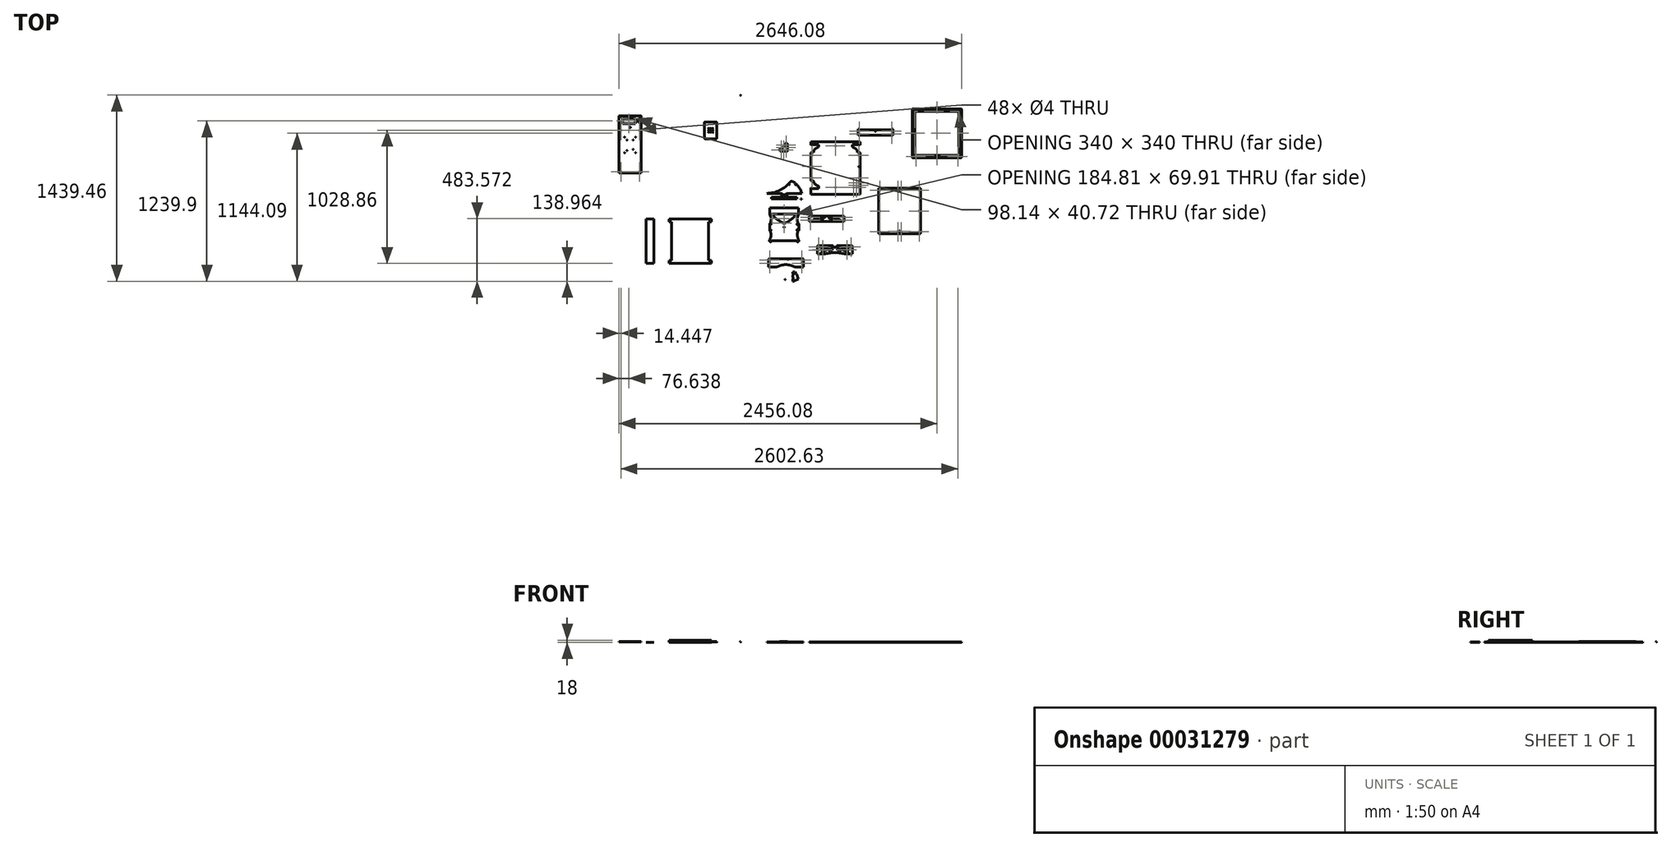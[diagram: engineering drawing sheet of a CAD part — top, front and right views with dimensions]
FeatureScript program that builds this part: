
annotation { "Feature Type Name" : "Feature", "Feature Type Description" : "" }
export const myFeature = defineFeature(function(context is Context, id is Id, definition is map)
    precondition{}
    {
        {
            var Q0;
            Q0=qCreatedBy(makeId("Top.planeOp"),FACE);
            var sketch = newSketch(context, id + "F0", { "sketchPlane" : qUnion([Q0])});
            skLineSegment(sketch, "E0", {"start": v(-196.4, -19.93) * mm, "end": v(-196.4, 30.07) * mm});
            skCircle(sketch, "E1", {"center": v(-187.75, 27.57) * mm, "radius": 2.75 * mm});
            skCircle(sketch, "E2", {"center": v(-187.75, -17.43) * mm, "radius": 2.75 * mm});
            skArc(sketch, "E3", {"start": v(-196.4, -19.93) * mm, "mid": v(-194.93, -23.47) * mm, "end": v(-191.4, -24.93) * mm});
            skArc(sketch, "E4", {"start": v(-191.4, 35.07) * mm, "mid": v(-194.93, 33.6) * mm, "end": v(-196.4, 30.07) * mm});
            skLineSegment(sketch, "E5", {"start": v(28.6, 30.07) * mm, "end": v(28.6, -19.93) * mm});
            skCircle(sketch, "E6", {"center": v(19.95, 27.57) * mm, "radius": 5.08 * mm});
            skCircle(sketch, "E7", {"center": v(19.95, -17.43) * mm, "radius": 5.08 * mm});
            skLineSegment(sketch, "E8.trimOffspring", {"start": v(14.88, 27.57) * mm, "end": v(19.95, 27.57) * mm});
            skPoint(sketch, "E9.visualSharp", {"position": v(28.6, 35.07) * mm});
            skArc(sketch, "E9.filletArc", {"start": v(28.6, 30.07) * mm, "mid": v(27.14, 33.6) * mm, "end": v(23.6, 35.07) * mm});
            skPoint(sketch, "E10.visualSharp", {"position": v(28.6, -24.93) * mm});
            skArc(sketch, "E10.filletArc", {"start": v(23.6, -24.93) * mm, "mid": v(27.14, -23.47) * mm, "end": v(28.6, -19.93) * mm});
            skCircle(sketch, "E11", {"center": v(-83.9, 5.07) * mm, "radius": 3.2 * mm});
            skLineSegment(sketch, "E12", {"start": v(-87.4, 19.55) * mm, "end": v(-80.33, 19.55) * mm});
            skLineSegment(sketch, "E13", {"start": v(-87.4, 21.55) * mm, "end": v(-80.33, 21.55) * mm});
            skLineSegment(sketch, "E14", {"start": v(-87.4, 23.86) * mm, "end": v(-80.32, 23.86) * mm});
            skLineSegment(sketch, "E15", {"start": v(-87.4, 25.86) * mm, "end": v(-80.32, 25.86) * mm});
            skLineSegment(sketch, "E16", {"start": v(-87.4, 27.93) * mm, "end": v(-80.32, 27.92) * mm});
            skLineSegment(sketch, "E17", {"start": v(-87.4, 31.34) * mm, "end": v(-80.31, 31.33) * mm});
            skLineSegment(sketch, "E18", {"start": v(-87.4, -9.95) * mm, "end": v(-80.38, -9.95) * mm});
            skLineSegment(sketch, "E19", {"start": v(-87.4, -11.95) * mm, "end": v(-80.38, -11.95) * mm});
            skLineSegment(sketch, "E20", {"start": v(-87.4, -16.14) * mm, "end": v(-80.39, -16.14) * mm});
            skLineSegment(sketch, "E21", {"start": v(-87.4, -14.14) * mm, "end": v(-80.39, -14.14) * mm});
            skLineSegment(sketch, "E22", {"start": v(-87.4, -21.89) * mm, "end": v(-80.4, -21.89) * mm});
            skLineSegment(sketch, "E23", {"start": v(-87.4, -18.45) * mm, "end": v(-80.4, -18.45) * mm});
            skLineSegment(sketch, "E24", {"start": v(-83.9, -21.89) * mm, "end": v(-80.4, -21.89) * mm});
            skLineSegment(sketch, "E25", {"start": v(-83.9, -21.89) * mm, "end": v(-87.4, -21.89) * mm});
            skLineSegment(sketch, "E26", {"start": v(-87.4, -21.89) * mm, "end": v(-87.4, -18.45) * mm});
            skLineSegment(sketch, "E27", {"start": v(-80.4, -21.89) * mm, "end": v(-80.4, -18.45) * mm});
            skLineSegment(sketch, "E28.trimOffspring", {"start": v(-87.4, 19.55) * mm, "end": v(-87.4, 21.55) * mm});
            skLineSegment(sketch, "E29.trimOffspring", {"start": v(-80.33, 19.55) * mm, "end": v(-80.33, 21.55) * mm});
            skLineSegment(sketch, "E30.trimOffspring", {"start": v(-80.32, 27.92) * mm, "end": v(-80.31, 31.34) * mm});
            skLineSegment(sketch, "E31.trimOffspring", {"start": v(-87.4, 27.93) * mm, "end": v(-87.4, 31.34) * mm});
            skLineSegment(sketch, "E32.trimOffspring", {"start": v(-87.4, 23.86) * mm, "end": v(-87.4, 25.86) * mm});
            skLineSegment(sketch, "E33.trimOffspring", {"start": v(-80.32, 23.86) * mm, "end": v(-80.32, 25.86) * mm});
            skLineSegment(sketch, "E34.trimOffspring", {"start": v(-87.4, -16.14) * mm, "end": v(-87.4, -14.14) * mm});
            skPoint(sketch, "E35.trimOffspring.end.orphan", {"position": v(-83.9, -24.93) * mm});
            skLineSegment(sketch, "E36.trimOffspring", {"start": v(-80.39, -16.14) * mm, "end": v(-80.39, -14.14) * mm});
            skLineSegment(sketch, "E37.trimOffspring", {"start": v(-87.4, -11.95) * mm, "end": v(-87.4, -9.95) * mm});
            skLineSegment(sketch, "E38.trimOffspring", {"start": v(-80.38, -11.95) * mm, "end": v(-80.38, -9.95) * mm});
            skCircle(sketch, "E39", {"center": v(-188.4, 109.57) * mm, "radius": 1.5 * mm});
            skCircle(sketch, "E40", {"center": v(20.6, 109.57) * mm, "radius": 1.5 * mm});
            skCircle(sketch, "E41", {"center": v(-188.4, -99.43) * mm, "radius": 1.5 * mm});
            skCircle(sketch, "E42", {"center": v(20.6, -99.43) * mm, "radius": 1.5 * mm});
            skLineSegment(sketch, "E43.MirrorCS", {"start": v(28.6, -19.93) * mm, "end": v(28.6, 30.07) * mm});
            skArc(sketch, "E44", {"start": v(-196.14, -94.85) * mm, "mid": v(-190.78, -108.11) * mm, "end": v(-179.4, -99.43) * mm});
            skArc(sketch, "E45", {"start": v(11.6, -99.43) * mm, "mid": v(22.98, -108.11) * mm, "end": v(28.34, -94.85) * mm});
            skArc(sketch, "E46", {"start": v(28.34, 104.98) * mm, "mid": v(22.98, 118.25) * mm, "end": v(11.6, 109.57) * mm});
            skArc(sketch, "E47", {"start": v(-179.4, 109.57) * mm, "mid": v(-190.78, 118.25) * mm, "end": v(-196.14, 104.98) * mm});
            skArc(sketch, "E48", {"start": v(-196.14, -94.85) * mm, "mid": v(-185.98, -60.42) * mm, "end": v(-191.4, -24.93) * mm});
            skArc(sketch, "E49", {"start": v(-83.9, -24.93) * mm, "mid": v(-137.85, -54.24) * mm, "end": v(-179.4, -99.43) * mm});
            skArc(sketch, "E50.MirrorCS", {"start": v(-83.9, -24.93) * mm, "mid": v(-29.95, -54.24) * mm, "end": v(11.6, -99.43) * mm});
            skArc(sketch, "E51.MirrorCS", {"start": v(28.34, -94.85) * mm, "mid": v(18.18, -60.42) * mm, "end": v(23.6, -24.93) * mm});
            skArc(sketch, "E52.MirrorCS", {"start": v(-83.9, 35.07) * mm, "mid": v(-137.85, 64.37) * mm, "end": v(-179.4, 109.57) * mm});
            skArc(sketch, "E53.MirrorCS", {"start": v(-196.14, 104.98) * mm, "mid": v(-185.98, 70.55) * mm, "end": v(-191.4, 35.07) * mm});
            skArc(sketch, "E54.MirrorCS", {"start": v(-83.9, 35.07) * mm, "mid": v(-29.95, 64.37) * mm, "end": v(11.6, 109.57) * mm});
            skArc(sketch, "E55.MirrorCS", {"start": v(28.34, 104.98) * mm, "mid": v(18.18, 70.55) * mm, "end": v(23.6, 35.07) * mm});
            skLineSegment(sketch, "E56.trimOffspring", {"start": v(-196.4, 5.07) * mm, "end": v(-227.61, 5.07) * mm});
            skLineSegment(sketch, "E57", {"start": v(-179.4, -99.43) * mm, "end": v(11.6, -99.43) * mm});
            skLineSegment(sketch, "E58", {"start": v(-179.4, 109.57) * mm, "end": v(11.6, 109.57) * mm});
            skLineSegment(sketch, "E59.bottom", {"start": v(-196.14, 104.98) * mm, "end": v(28.34, 104.98) * mm});
            skLineSegment(sketch, "E59.top", {"start": v(-196.14, 155.03) * mm, "end": v(28.34, 155.03) * mm});
            skLineSegment(sketch, "E59.left", {"start": v(-196.14, 104.98) * mm, "end": v(-196.14, 155.03) * mm});
            skLineSegment(sketch, "E59.right", {"start": v(28.34, 104.98) * mm, "end": v(28.34, 155.03) * mm});
            skSolve(sketch);
        }
        {
            var Q0;
            Q0=makeQuery(id+"F0.imprint","IMPRINT",FACE,{"disambiguationData":[TD([[makeQuery(id+"F0.imprint","IMPRINT",EDGE,{"derivedFrom":sQuery(id+"F0.wireOp",EDGE,"E0")}),-1.0]])]});
            var Q1;
            Q1=makeQuery(id+"F0.imprint","IMPRINT",FACE,{"disambiguationData":[TD([[makeQuery(id+"F0.imprint","IMPRINT",EDGE,{"derivedFrom":sQuery(id+"F0.wireOp",EDGE,"E23")}),-1.0]])]});
            var Q2;
            Q2=makeQuery(id+"F0.imprint","IMPRINT",FACE,{"disambiguationData":[TD([[makeQuery(id+"F0.imprint","IMPRINT",EDGE,{"derivedFrom":sQuery(id+"F0.wireOp",EDGE,"E49")}),1.0]])]});
            var Q3;
            Q3=makeQuery(id+"F0.imprint","IMPRINT",FACE,{"disambiguationData":[TD([[makeQuery(id+"F0.imprint","IMPRINT",EDGE,{"derivedFrom":sQuery(id+"F0.wireOp",EDGE,"E18")}),-1.0]])]});
            var Q4;
            Q4=makeQuery(id+"F0.imprint","IMPRINT",FACE,{"disambiguationData":[TD([[makeQuery(id+"F0.imprint","IMPRINT",EDGE,{"derivedFrom":sQuery(id+"F0.wireOp",EDGE,"E20")}),1.0]])]});
            var Q5;
            Q5=makeQuery(id+"F0.imprint","IMPRINT",FACE,{"disambiguationData":[TD([[makeQuery(id+"F0.imprint","IMPRINT",EDGE,{"derivedFrom":sQuery(id+"F0.wireOp",EDGE,"E52.MirrorCS")}),-1.0]])]});
            var Q6;
            Q6=makeQuery(id+"F0.imprint","IMPRINT",FACE,{"disambiguationData":[TD([[makeQuery(id+"F0.imprint","IMPRINT",EDGE,{"derivedFrom":sQuery(id+"F0.wireOp",EDGE,"E12")}),1.0]])]});
            var Q7;
            Q7=makeQuery(id+"F0.imprint","IMPRINT",FACE,{"disambiguationData":[TD([[makeQuery(id+"F0.imprint","IMPRINT",EDGE,{"derivedFrom":sQuery(id+"F0.wireOp",EDGE,"E14")}),1.0]])]});
            var Q8;
            {var subQ2=sQuery(id+"F0.wireOp",EDGE,"E16");Q8=makeQuery(id+"F0.imprint","IMPRINT",FACE,{"disambiguationData":[TD([[makeQuery(id+"F0.imprint","IMPRINT",EDGE,{"derivedFrom":subQ2}),1.0]])]});}
            var Q9;
            {var subQ7=sQuery(id+"F0.wireOp",EDGE,"E58");Q9=makeQuery(id+"F0.imprint","IMPRINT",FACE,{"disambiguationData":[TD([[makeQuery(id+"F0.imprint","IMPRINT",EDGE,{"derivedFrom":subQ7}),1.0]])]});}
            var Q10;
            Q10=makeQuery(id+"F0.imprint","IMPRINT",FACE,{"disambiguationData":[TD([[makeQuery(id+"F0.imprint","IMPRINT",EDGE,{"derivedFrom":sQuery(id+"F0.wireOp",EDGE,"E40")}),-1.0]])]});
            var Q11;
            Q11=makeQuery(id+"F0.imprint","IMPRINT",FACE,{"disambiguationData":[TD([[makeQuery(id+"F0.imprint","IMPRINT",EDGE,{"derivedFrom":sQuery(id+"F0.wireOp",EDGE,"E39")}),-1.0]])]});
            var Q12;
            {var subQ5=sQuery(id+"F0.wireOp",EDGE,"E58");Q12=makeQuery(id+"F0.imprint","IMPRINT",FACE,{"disambiguationData":[TD([[makeQuery(id+"F0.imprint","IMPRINT",EDGE,{"derivedFrom":subQ5}),-1.0]])]});}
            extrude(context, id + "F1", {"entities" : qUnion([Q0, Q1, Q2, Q3, Q4, Q5, Q6, Q7, Q8, Q9, Q10, Q11, Q12]), "depth" : 4 * mm});
        }
        {
            var Q0;
            Q0=qCreatedBy(makeId("Top.planeOp"),FACE);
            var sketch = newSketch(context, id + "F2", { "sketchPlane" : qUnion([Q0])});
            skLineSegment(sketch, "E60", {"start": v(-104.69, 266.67) * mm, "end": v(-62.63, 266.67) * mm});
            skLineSegment(sketch, "E61", {"start": v(-62.63, 266.67) * mm, "end": v(-62.63, 266.67) * mm});
            skLineSegment(sketch, "E62", {"start": v(-62.63, 266.67) * mm, "end": v(51.38, 266.67) * mm});
            skLineSegment(sketch, "E63", {"start": v(51.38, 266.67) * mm, "end": v(51.38, 224.88) * mm});
            skLineSegment(sketch, "E64", {"start": v(51.38, 224.88) * mm, "end": v(41.38, 224.88) * mm});
            skLineSegment(sketch, "E65", {"start": v(41.38, 224.88) * mm, "end": v(51.38, 224.88) * mm});
            skLineSegment(sketch, "E66.bottom", {"start": v(-104.69, 266.67) * mm, "end": v(-62.62, 266.67) * mm});
            skLineSegment(sketch, "E66.right", {"start": v(-62.62, 266.67) * mm, "end": v(-62.62, 224.88) * mm});
            skLineSegment(sketch, "E67", {"start": v(-104.69, 224.88) * mm, "end": v(-62.62, 224.88) * mm});
            skLineSegment(sketch, "E68", {"start": v(-62.62, 224.88) * mm, "end": v(41.38, 224.88) * mm});
            skLineSegment(sketch, "E69", {"start": v(-104.69, 224.88) * mm, "end": v(-104.69, 266.67) * mm});
            skCircle(sketch, "E70", {"center": v(41.38, 258.88) * mm, "radius": 2 * mm});
            skCircle(sketch, "E71", {"center": v(41.38, 234.88) * mm, "radius": 2 * mm});
            skCircle(sketch, "E72", {"center": v(-83.65, 245.28) * mm, "radius": 11.05 * mm});
            skCircle(sketch, "E73", {"center": v(-99.2, 229.73) * mm, "radius": 1.65 * mm});
            skCircle(sketch, "E74", {"center": v(-68.1, 229.79) * mm, "radius": 1.65 * mm});
            skCircle(sketch, "E75", {"center": v(-99.2, 260.83) * mm, "radius": 1.65 * mm});
            skCircle(sketch, "E76", {"center": v(-68.1, 261) * mm, "radius": 1.65 * mm});
            skLineSegment(sketch, "E77", {"start": v(-83.66, 224.88) * mm, "end": v(-83.66, 266.67) * mm});
            skLineSegment(sketch, "E78.MirrorCS", {"start": v(-104.69, 224.88) * mm, "end": v(-208.69, 224.88) * mm});
            skLineSegment(sketch, "E79.MirrorCS", {"start": v(-104.69, 266.67) * mm, "end": v(-218.69, 266.67) * mm});
            skLineSegment(sketch, "E80.MirrorCS", {"start": v(-218.69, 266.67) * mm, "end": v(-218.69, 224.88) * mm});
            skLineSegment(sketch, "E81.MirrorCS", {"start": v(-208.69, 224.88) * mm, "end": v(-210.69, 224.88) * mm});
            skCircle(sketch, "E82.MirrorC", {"center": v(-208.69, 234.88) * mm, "radius": 2 * mm});
            skCircle(sketch, "E83.MirrorC", {"center": v(-208.69, 258.88) * mm, "radius": 2 * mm});
            skLineSegment(sketch, "E84.bottom", {"start": v(-83.66, 224.88) * mm, "end": v(-181, 224.88) * mm});
            skLineSegment(sketch, "E84.top", {"start": v(-83.66, 237.25) * mm, "end": v(-181, 237.25) * mm});
            skLineSegment(sketch, "E84.left", {"start": v(-83.66, 224.88) * mm, "end": v(-83.66, 237.25) * mm});
            skLineSegment(sketch, "E84.right", {"start": v(-181, 224.88) * mm, "end": v(-181, 237.25) * mm});
            skLineSegment(sketch, "E85.MirrorCS", {"start": v(-83.66, 237.25) * mm, "end": v(13.7, 237.25) * mm});
            skLineSegment(sketch, "E86.MirrorCS", {"start": v(13.7, 224.88) * mm, "end": v(13.7, 237.25) * mm});
            skCircle(sketch, "E87", {"center": v(3.35, 260.88) * mm, "radius": 1.5 * mm});
            skCircle(sketch, "E88", {"center": v(-44.47, 253.5) * mm, "radius": 1.5 * mm});
            skCircle(sketch, "E89", {"center": v(-44.78, 334.21) * mm, "radius": 1.5 * mm});
            skCircle(sketch, "E90", {"center": v(3.26, 334.22) * mm, "radius": 1.5 * mm});
            skArc(sketch, "E91", {"start": v(51.38, 266.67) * mm, "mid": v(26.53, 319.96) * mm, "end": v(-18.2, 358.13) * mm});
            skArc(sketch, "E92", {"start": v(-218.69, 266.67) * mm, "mid": v(-117.85, 289.71) * mm, "end": v(-37.02, 354.25) * mm});
            skArc(sketch, "E93.filletArc", {"start": v(-18.2, 358.13) * mm, "mid": v(-28.3, 359.6) * mm, "end": v(-37.02, 354.25) * mm});
            skLineSegment(sketch, "E94", {"start": v(-218.69, 224.88) * mm, "end": v(-218.69, 220.88) * mm});
            skLineSegment(sketch, "E95", {"start": v(-218.69, 220.88) * mm, "end": v(-210.69, 220.88) * mm});
            skLineSegment(sketch, "E96", {"start": v(-210.69, 220.88) * mm, "end": v(-210.69, 224.88) * mm});
            skLineSegment(sketch, "E97.MirrorCS", {"start": v(51.38, 224.88) * mm, "end": v(51.38, 220.88) * mm});
            skLineSegment(sketch, "E98.MirrorCS", {"start": v(43.38, 220.88) * mm, "end": v(43.38, 224.88) * mm});
            skLineSegment(sketch, "E99.MirrorCS", {"start": v(51.38, 220.88) * mm, "end": v(43.38, 220.88) * mm});
            skPoint(sketch, "E100.orphan", {"position": v(-218.69, 224.88) * mm});
            skSolve(sketch);
        }
        {
            var Q0;
            {var subQ8=sQuery(id+"F2.wireOp",EDGE,"E62");Q0=makeQuery(id+"F2.imprint","IMPRINT",FACE,{"disambiguationData":[TD([[makeQuery(id+"F2.imprint","IMPRINT",EDGE,{"derivedFrom":subQ8}),1.0]])]});}
            var Q1;
            Q1=makeQuery(id+"F2.imprint","IMPRINT",FACE,{"disambiguationData":[TD([[makeQuery(id+"F2.imprint","IMPRINT",EDGE,{"derivedFrom":sQuery(id+"F2.wireOp",EDGE,"E78.MirrorCS")}),-1.0]])]});
            var Q2;
            Q2=makeQuery(id+"F2.imprint","IMPRINT",FACE,{"disambiguationData":[TD([[makeQuery(id+"F2.imprint","IMPRINT",EDGE,{"derivedFrom":sQuery(id+"F2.wireOp",EDGE,"E73")}),-1.0]])]});
            var Q3;
            Q3=makeQuery(id+"F2.imprint","IMPRINT",FACE,{"disambiguationData":[TD([[makeQuery(id+"F2.imprint","IMPRINT",EDGE,{"derivedFrom":sQuery(id+"F2.wireOp",EDGE,"E74")}),-1.0]])]});
            var Q4;
            {var subQ1=sQuery(id+"F2.wireOp",EDGE,"E97.MirrorCS");Q4=makeQuery(id+"F2.imprint","IMPRINT",FACE,{"disambiguationData":[TD([[makeQuery(id+"F2.imprint","IMPRINT",EDGE,{"derivedFrom":subQ1}),-1.0]])]});}
            var Q5;
            Q5=makeQuery(id+"F2.imprint","IMPRINT",FACE,{"disambiguationData":[TD([[makeQuery(id+"F2.imprint","IMPRINT",EDGE,{"derivedFrom":sQuery(id+"F2.wireOp",EDGE,"E75")}),-1.0]])]});
            var Q6;
            Q6=makeQuery(id+"F2.imprint","IMPRINT",FACE,{"disambiguationData":[TD([[makeQuery(id+"F2.imprint","IMPRINT",EDGE,{"derivedFrom":sQuery(id+"F2.wireOp",EDGE,"E76")}),-1.0]])]});
            var Q7;
            {var subQ5=sQuery(id+"F2.wireOp",EDGE,"E86.MirrorCS");Q7=makeQuery(id+"F2.imprint","IMPRINT",FACE,{"disambiguationData":[TD([[makeQuery(id+"F2.imprint","IMPRINT",EDGE,{"derivedFrom":subQ5}),1.0]])]});}
            var Q8;
            {var subQ5=sQuery(id+"F2.wireOp",EDGE,"E84.right");Q8=makeQuery(id+"F2.imprint","IMPRINT",FACE,{"disambiguationData":[TD([[makeQuery(id+"F2.imprint","IMPRINT",EDGE,{"derivedFrom":subQ5}),-1.0]])]});}
            var Q9;
            {var subQ7=sQuery(id+"F2.wireOp",EDGE,"E62");Q9=makeQuery(id+"F2.imprint","IMPRINT",FACE,{"disambiguationData":[TD([[makeQuery(id+"F2.imprint","IMPRINT",EDGE,{"derivedFrom":subQ7}),-1.0]])]});}
            extrude(context, id + "F3", {"entities" : qUnion([Q0, Q1, Q2, Q3, Q4, Q5, Q6, Q7, Q8, Q9]), "depth" : 4 * mm});
        }
        {
            var Q0;
            Q0=qCreatedBy(makeId("Top.planeOp"),FACE);
            var sketch = newSketch(context, id + "F4", { "sketchPlane" : qUnion([Q0])});
            skLineSegment(sketch, "E101", {"start": v(600.2, 758.38) * mm, "end": v(642.2, 758.38) * mm});
            skLineSegment(sketch, "E102", {"start": v(642.2, 758.38) * mm, "end": v(642.2, 758.38) * mm});
            skLineSegment(sketch, "E103", {"start": v(642.2, 758.38) * mm, "end": v(748.23, 758.38) * mm});
            skLineSegment(sketch, "E104", {"start": v(756.23, 758.38) * mm, "end": v(756.23, 716.59) * mm});
            skLineSegment(sketch, "E105", {"start": v(756.23, 716.59) * mm, "end": v(746.23, 716.59) * mm});
            skLineSegment(sketch, "E106", {"start": v(746.23, 716.59) * mm, "end": v(756.23, 716.59) * mm});
            skLineSegment(sketch, "E107.bottom", {"start": v(600.2, 758.38) * mm, "end": v(642.26, 758.38) * mm});
            skLineSegment(sketch, "E107.right", {"start": v(642.26, 758.38) * mm, "end": v(642.26, 716.59) * mm});
            skLineSegment(sketch, "E108", {"start": v(600.2, 716.59) * mm, "end": v(642.26, 716.59) * mm});
            skLineSegment(sketch, "E109", {"start": v(642.26, 716.59) * mm, "end": v(746.23, 716.59) * mm});
            skLineSegment(sketch, "E110", {"start": v(600.2, 716.59) * mm, "end": v(600.2, 758.38) * mm});
            skCircle(sketch, "E111", {"center": v(746.23, 747.66) * mm, "radius": 2 * mm});
            skCircle(sketch, "E112", {"center": v(746.23, 725.6) * mm, "radius": 2 * mm});
            skLineSegment(sketch, "E113", {"start": v(621.23, 716.59) * mm, "end": v(621.23, 758.38) * mm});
            skLineSegment(sketch, "E114.MirrorCS", {"start": v(600.2, 716.59) * mm, "end": v(496.23, 716.59) * mm});
            skLineSegment(sketch, "E115.MirrorCS", {"start": v(600.26, 758.38) * mm, "end": v(494.23, 758.38) * mm});
            skLineSegment(sketch, "E116.MirrorCS", {"start": v(486.23, 758.38) * mm, "end": v(486.23, 716.59) * mm});
            skLineSegment(sketch, "E117.MirrorCS", {"start": v(496.23, 716.59) * mm, "end": v(486.23, 716.59) * mm});
            skCircle(sketch, "E118.MirrorC", {"center": v(496.23, 725.6) * mm, "radius": 2 * mm});
            skCircle(sketch, "E119.MirrorC", {"center": v(496.23, 747.66) * mm, "radius": 2 * mm});
            skCircle(sketch, "E120", {"center": v(621.23, 746.98) * mm, "radius": 1.5 * mm});
            skPoint(sketch, "E121", {"position": v(494.23, 758.38) * mm});
            skPoint(sketch, "E122", {"position": v(735, 758.38) * mm});
            skLineSegment(sketch, "E123", {"start": v(486.23, 758.38) * mm, "end": v(486.23, 762.38) * mm});
            skLineSegment(sketch, "E124", {"start": v(486.23, 762.38) * mm, "end": v(494.23, 762.38) * mm});
            skLineSegment(sketch, "E125", {"start": v(494.23, 762.38) * mm, "end": v(494.23, 758.38) * mm});
            skLineSegment(sketch, "E126.MirrorCS", {"start": v(756.23, 762.38) * mm, "end": v(748.23, 762.38) * mm});
            skLineSegment(sketch, "E127.MirrorCS", {"start": v(756.23, 758.38) * mm, "end": v(756.23, 762.38) * mm});
            skLineSegment(sketch, "E128.MirrorCS", {"start": v(748.23, 762.38) * mm, "end": v(748.23, 758.38) * mm});
            skSolve(sketch);
        }
        {
            var Q0;
            Q0=makeQuery(id+"F4.imprint","IMPRINT",FACE,{"disambiguationData":[TD([[makeQuery(id+"F4.imprint","IMPRINT",EDGE,{"derivedFrom":sQuery(id+"F4.wireOp",EDGE,"E103")}),-1.0]])]});
            var Q1;
            {var subQ8=sQuery(id+"F4.wireOp",EDGE,"E107.right");Q1=makeQuery(id+"F4.imprint","IMPRINT",FACE,{"disambiguationData":[TD([[makeQuery(id+"F4.imprint","IMPRINT",EDGE,{"derivedFrom":subQ8}),-1.0]])]});}
            var Q2;
            {var subQ5=sQuery(id+"F4.wireOp",EDGE,"E110");Q2=makeQuery(id+"F4.imprint","IMPRINT",FACE,{"disambiguationData":[TD([[makeQuery(id+"F4.imprint","IMPRINT",EDGE,{"derivedFrom":subQ5}),-1.0]])]});}
            var Q3;
            {var subQ2=sQuery(id+"F4.wireOp",EDGE,"E110");Q3=makeQuery(id+"F4.imprint","IMPRINT",FACE,{"disambiguationData":[TD([[makeQuery(id+"F4.imprint","IMPRINT",EDGE,{"derivedFrom":subQ2}),1.0]])]});}
            extrude(context, id + "F5", {"entities" : qUnion([Q0, Q1, Q2, Q3]), "depth" : 4 * mm});
        }
        {
            var Q0;
            Q0=qCreatedBy(makeId("Top.planeOp"),FACE);
            var sketch = newSketch(context, id + "F6", { "sketchPlane" : qUnion([Q0])});
            skLineSegment(sketch, "E129", {"start": v(63.81, -240.59) * mm, "end": v(63.81, -260.59) * mm});
            skCircle(sketch, "E130", {"center": v(53.81, -250.59) * mm, "radius": 2 * mm});
            skCircle(sketch, "E131.MirrorC", {"center": v(-196.26, -250.59) * mm, "radius": 2 * mm});
            skCircle(sketch, "E132", {"center": v(-196.26, -274.59) * mm, "radius": 2 * mm});
            skCircle(sketch, "E133.MirrorC", {"center": v(53.81, -274.59) * mm, "radius": 2 * mm});
            skCircle(sketch, "E134", {"center": v(-76.65, -399.92) * mm, "radius": 1.75 * mm});
            skCircle(sketch, "E135", {"center": v(-76.65, -349.92) * mm, "radius": 1.75 * mm});
            skCircle(sketch, "E136", {"center": v(-221.83, -399.92) * mm, "radius": 1.75 * mm});
            skCircle(sketch, "E137", {"center": v(-221.65, -349.97) * mm, "radius": 1.75 * mm});
            skPoint(sketch, "E138", {"position": v(63.81, -264.59) * mm});
            skLineSegment(sketch, "E139", {"start": v(63.81, -264.59) * mm, "end": v(55.81, -264.59) * mm});
            skLineSegment(sketch, "E140", {"start": v(55.81, -264.59) * mm, "end": v(55.81, -260.59) * mm});
            skLineSegment(sketch, "E141", {"start": v(55.81, -260.59) * mm, "end": v(63.81, -260.59) * mm});
            skLineSegment(sketch, "E142.MirrorCS", {"start": v(-206.26, -264.59) * mm, "end": v(-198.26, -264.59) * mm});
            skLineSegment(sketch, "E143.MirrorCS", {"start": v(-198.26, -264.59) * mm, "end": v(-198.26, -260.59) * mm});
            skLineSegment(sketch, "E144.MirrorCS", {"start": v(-198.26, -260.59) * mm, "end": v(-206.26, -260.59) * mm});
            skCircle(sketch, "E145.MirrorC", {"center": v(-86.96, -378.05) * mm, "radius": 10 * mm});
            skLineSegment(sketch, "E146.trimOffspring", {"start": v(-206.26, -264.59) * mm, "end": v(-206.26, -304.59) * mm});
            skLineSegment(sketch, "E147.trimOffspring", {"start": v(63.81, -264.59) * mm, "end": v(63.81, -304.59) * mm});
            skLineSegment(sketch, "E148", {"start": v(-206.26, -260.59) * mm, "end": v(-206.26, -240.59) * mm});
            skLineSegment(sketch, "E149", {"start": v(63.81, -240.59) * mm, "end": v(-206.26, -240.59) * mm});
            skLineSegment(sketch, "E150", {"start": v(-206.26, -304.59) * mm, "end": v(-144.26, -304.59) * mm});
            skLineSegment(sketch, "E151", {"start": v(1.81, -304.59) * mm, "end": v(63.81, -304.59) * mm});
            skLineSegment(sketch, "E152.bottom", {"start": v(-230, -345.8) * mm, "end": v(-68.48, -345.8) * mm});
            skLineSegment(sketch, "E152.top", {"start": v(-230, -417.83) * mm, "end": v(-68.48, -417.83) * mm});
            skLineSegment(sketch, "E152.right", {"start": v(-68.48, -345.8) * mm, "end": v(-68.48, -356.82) * mm});
            skCircle(sketch, "E153", {"center": v(-54.27, -294.37) * mm, "radius": 1.75 * mm});
            skCircle(sketch, "E154", {"center": v(-54.27, -244.37) * mm, "radius": 1.75 * mm});
            skArc(sketch, "E155", {"start": v(1.81, -304.59) * mm, "mid": v(-71.22, -285.2) * mm, "end": v(-144.26, -304.59) * mm});
            skLineSegment(sketch, "E156", {"start": v(-68.48, -399.92) * mm, "end": v(-64.48, -399.92) * mm});
            skLineSegment(sketch, "E157", {"start": v(-68.48, -385.74) * mm, "end": v(-64.48, -385.74) * mm});
            skLineSegment(sketch, "E158", {"start": v(-68.48, -356.82) * mm, "end": v(-64.48, -356.82) * mm});
            skLineSegment(sketch, "E159", {"start": v(-68.48, -370.31) * mm, "end": v(-64.48, -370.31) * mm});
            skLineSegment(sketch, "E160.trimOffspring", {"start": v(-68.48, -370.31) * mm, "end": v(-68.48, -385.74) * mm});
            skLineSegment(sketch, "E161.trimOffspring", {"start": v(-68.48, -399.92) * mm, "end": v(-68.48, -417.83) * mm});
            skLineSegment(sketch, "E162.MirrorCS", {"start": v(-12.72, -366.04) * mm, "end": v(-12.72, -352.54) * mm});
            skLineSegment(sketch, "E163.MirrorCS", {"start": v(-16.72, -395.64) * mm, "end": v(-12.72, -395.64) * mm});
            skLineSegment(sketch, "E164.MirrorCS", {"start": v(-12.72, -395.64) * mm, "end": v(-12.72, -381.46) * mm});
            skLineSegment(sketch, "E165.MirrorCS", {"start": v(-16.72, -381.46) * mm, "end": v(-12.72, -381.46) * mm});
            skLineSegment(sketch, "E166", {"start": v(-12.72, -366.04) * mm, "end": v(-16.72, -366.04) * mm});
            skLineSegment(sketch, "E167", {"start": v(-12.72, -352.54) * mm, "end": v(-16.72, -352.54) * mm});
            skLineSegment(sketch, "E168", {"start": v(-16.72, -352.54) * mm, "end": v(-12.72, -352.54) * mm});
            skLineSegment(sketch, "E169", {"start": v(-16.72, -408.89) * mm, "end": v(-16.72, -395.64) * mm});
            skLineSegment(sketch, "E170", {"start": v(-12.72, -340.89) * mm, "end": v(-16.72, -340.89) * mm});
            skLineSegment(sketch, "E171", {"start": v(-16.72, -381.46) * mm, "end": v(-16.72, -366.04) * mm});
            skLineSegment(sketch, "E172", {"start": v(-16.72, -352.54) * mm, "end": v(-16.72, -340.89) * mm});
            skArc(sketch, "E173", {"start": v(-64.48, -415.8) * mm, "mid": v(-44.88, -381.81) * mm, "end": v(-64.48, -347.82) * mm});
            skLineSegment(sketch, "E174", {"start": v(-64.48, -399.92) * mm, "end": v(-64.48, -415.8) * mm});
            skLineSegment(sketch, "E175", {"start": v(-64.48, -385.74) * mm, "end": v(-64.48, -370.31) * mm});
            skLineSegment(sketch, "E176.trimOffspring", {"start": v(-64.48, -356.82) * mm, "end": v(-64.48, -347.82) * mm});
            skLineSegment(sketch, "E177", {"start": v(-221.83, -399.92) * mm, "end": v(-76.65, -399.92) * mm, "construction": true});
            skLineSegment(sketch, "E178", {"start": v(-149.24, -399.92) * mm, "end": v(-149.24, -377.49) * mm, "construction": true});
            skLineSegment(sketch, "E179.MirrorCS", {"start": v(-230, -399.92) * mm, "end": v(-230, -417.83) * mm});
            skLineSegment(sketch, "E180.MirrorCS", {"start": v(-234, -399.92) * mm, "end": v(-234, -415.8) * mm});
            skLineSegment(sketch, "E181.MirrorCS", {"start": v(-230, -399.92) * mm, "end": v(-234, -399.92) * mm});
            skLineSegment(sketch, "E182.MirrorCS", {"start": v(-230, -370.31) * mm, "end": v(-230, -385.74) * mm});
            skLineSegment(sketch, "E183.MirrorCS", {"start": v(-234, -385.74) * mm, "end": v(-234, -370.31) * mm});
            skLineSegment(sketch, "E184.MirrorCS", {"start": v(-230, -370.31) * mm, "end": v(-234, -370.31) * mm});
            skLineSegment(sketch, "E185.MirrorCS", {"start": v(-230, -345.8) * mm, "end": v(-230, -356.82) * mm});
            skLineSegment(sketch, "E186.MirrorCS", {"start": v(-234, -356.82) * mm, "end": v(-234, -347.82) * mm});
            skArc(sketch, "E187.MirrorCS", {"start": v(-234, -415.8) * mm, "mid": v(-253.6, -381.81) * mm, "end": v(-234, -347.82) * mm});
            skLineSegment(sketch, "E188.MirrorCS", {"start": v(-230, -385.74) * mm, "end": v(-234, -385.74) * mm});
            skLineSegment(sketch, "E189.MirrorCS", {"start": v(-230, -356.82) * mm, "end": v(-234, -356.82) * mm});
            skLineSegment(sketch, "E190", {"start": v(-1.23, -340.89) * mm, "end": v(-12.72, -340.89) * mm});
            skLineSegment(sketch, "E191", {"start": v(-16.72, -395.64) * mm, "end": v(-16.72, -413.55) * mm});
            skLineSegment(sketch, "E192", {"start": v(-12.72, -413.55) * mm, "end": v(-16.72, -413.55) * mm});
            skLineSegment(sketch, "E193", {"start": v(-12.72, -413.55) * mm, "end": v(25.7, -394.12) * mm});
            skPoint(sketch, "E194.start.orphan", {"position": v(-1.23, -340.89) * mm});
            skLineSegment(sketch, "E195", {"start": v(-1.23, -340.89) * mm, "end": v(7.72, -358.58) * mm});
            skLineSegment(sketch, "E196", {"start": v(15.8, -365.7) * mm, "end": v(11.29, -356.78) * mm});
            skLineSegment(sketch, "E197", {"start": v(11.29, -356.78) * mm, "end": v(7.72, -358.58) * mm});
            skLineSegment(sketch, "E198", {"start": v(15.8, -365.7) * mm, "end": v(20.31, -374.62) * mm});
            skLineSegment(sketch, "E199", {"start": v(20.31, -374.62) * mm, "end": v(16.74, -376.43) * mm});
            skLineSegment(sketch, "E200.trimOffspring", {"start": v(16.74, -376.43) * mm, "end": v(25.7, -394.12) * mm});
            skLineSegment(sketch, "E201", {"start": v(-64.48, -385.74) * mm, "end": v(-56.77, -385.74) * mm, "construction": true});
            skArc(sketch, "E202", {"start": v(-52.77, -381.74) * mm, "mid": v(-54.77, -379.74) * mm, "end": v(-56.77, -381.74) * mm});
            skArc(sketch, "E203.MirrorC", {"start": v(-52.77, -385.74) * mm, "mid": v(-54.77, -387.74) * mm, "end": v(-56.77, -385.74) * mm});
            skLineSegment(sketch, "E204", {"start": v(-52.77, -385.74) * mm, "end": v(-52.77, -381.74) * mm});
            skLineSegment(sketch, "E205", {"start": v(-56.77, -381.74) * mm, "end": v(-56.77, -385.74) * mm});
            skArc(sketch, "E206.MirrorCS", {"start": v(-245.71, -385.74) * mm, "mid": v(-243.71, -387.74) * mm, "end": v(-241.71, -385.74) * mm});
            skLineSegment(sketch, "E207.MirrorCS", {"start": v(-245.71, -385.74) * mm, "end": v(-245.71, -381.74) * mm});
            skArc(sketch, "E208.MirrorCS", {"start": v(-245.71, -381.74) * mm, "mid": v(-243.71, -379.74) * mm, "end": v(-241.71, -381.74) * mm});
            skLineSegment(sketch, "E209.MirrorCS", {"start": v(-241.71, -381.74) * mm, "end": v(-241.71, -385.74) * mm});
            skPoint(sketch, "E210", {"position": v(-54.75, -385.74) * mm});
            skLineSegment(sketch, "E211.bottom", {"start": v(-210.56, -361.3) * mm, "end": v(-112.3, -361.3) * mm});
            skLineSegment(sketch, "E211.top", {"start": v(-210.56, -402.02) * mm, "end": v(-112.3, -402.02) * mm});
            skLineSegment(sketch, "E211.left", {"start": v(-210.56, -361.3) * mm, "end": v(-210.56, -402.02) * mm});
            skLineSegment(sketch, "E211.right", {"start": v(-112.3, -361.3) * mm, "end": v(-112.3, -402.02) * mm});
            skSolve(sketch);
        }
        {
            var Q0;
            Q0=makeQuery(id+"F6.imprint","IMPRINT",FACE,{"disambiguationData":[TD([[makeQuery(id+"F6.imprint","IMPRINT",EDGE,{"derivedFrom":sQuery(id+"F6.wireOp",EDGE,"E129")}),-1.0]])]});
            var Q1;
            Q1=makeQuery(id+"F6.imprint","IMPRINT",FACE,{"disambiguationData":[TD([[makeQuery(id+"F6.imprint","IMPRINT",EDGE,{"derivedFrom":sQuery(id+"F6.wireOp",EDGE,"E134")}),1.0]])]});
            var Q2;
            Q2=makeQuery(id+"F6.imprint","IMPRINT",FACE,{"disambiguationData":[TD([[makeQuery(id+"F6.imprint","IMPRINT",EDGE,{"derivedFrom":sQuery(id+"F6.wireOp",EDGE,"2918f89a-1ed2-4754-b867-7cf13f7856ee")}),-1.0]])]});
            var Q3;
            Q3=makeQuery(id+"F6.imprint","IMPRINT",FACE,{"disambiguationData":[TD([[makeQuery(id+"F6.imprint","IMPRINT",EDGE,{"derivedFrom":sQuery(id+"F6.wireOp",EDGE,"2918f89a-1ed2-4754-b867-7cf13f7856ee")}),1.0]])]});
            var Q4;
            Q4=makeQuery(id+"F6.imprint","IMPRINT",FACE,{"disambiguationData":[TD([[makeQuery(id+"F6.imprint","IMPRINT",EDGE,{"derivedFrom":sQuery(id+"F6.wireOp",EDGE,"E162.MirrorCS")}),-1.0]])]});
            extrude(context, id + "F7", {"entities" : qUnion([Q0, Q1, Q2, Q3, Q4]), "depth" : 4 * mm});
        }
        {
            var Q0;
            Q0=qCreatedBy(makeId("Top.planeOp"),FACE);
            var sketch = newSketch(context, id + "F8", { "sketchPlane" : qUnion([Q0])});
            skLineSegment(sketch, "E212.MirrorCS", {"start": v(234.93, -201.78) * mm, "end": v(182.93, -201.78) * mm});
            skLineSegment(sketch, "E213.MirrorCS", {"start": v(294.45, -137.78) * mm, "end": v(172.93, -137.78) * mm});
            skCircle(sketch, "E214", {"center": v(182.93, -171.78) * mm, "radius": 2 * mm});
            skArc(sketch, "E215", {"start": v(381, -201.78) * mm, "mid": v(307.96, -191.74) * mm, "end": v(234.93, -201.78) * mm});
            skLineSegment(sketch, "E216", {"start": v(321.48, -137.78) * mm, "end": v(443, -137.78) * mm});
            skLineSegment(sketch, "E217", {"start": v(381, -201.78) * mm, "end": v(433, -201.78) * mm});
            skLineSegment(sketch, "E218.MirrorCS", {"start": v(172.93, -137.78) * mm, "end": v(172.93, -157.78) * mm});
            skCircle(sketch, "E219.MirrorC", {"center": v(433, -171.78) * mm, "radius": 2 * mm});
            skLineSegment(sketch, "E220.MirrorCS", {"start": v(182.93, -201.78) * mm, "end": v(172.93, -201.78) * mm});
            skCircle(sketch, "E221.MirrorC", {"center": v(182.93, -147.78) * mm, "radius": 2 * mm});
            skLineSegment(sketch, "E222", {"start": v(443, -137.78) * mm, "end": v(443, -157.78) * mm});
            skCircle(sketch, "E223", {"center": v(433, -147.78) * mm, "radius": 2 * mm});
            skLineSegment(sketch, "E224", {"start": v(433, -201.78) * mm, "end": v(443, -201.78) * mm});
            skLineSegment(sketch, "E225", {"start": v(443, -201.78) * mm, "end": v(433, -201.78) * mm});
            skLineSegment(sketch, "E226", {"start": v(182.93, -201.78) * mm, "end": v(192.93, -201.78) * mm});
            skLineSegment(sketch, "E227.0", {"start": v(217.13, -158.47) * mm, "end": v(213.2, -166.38) * mm});
            skLineSegment(sketch, "E227.1", {"start": v(213.2, -166.38) * mm, "end": v(204.38, -166.93) * mm});
            skLineSegment(sketch, "E227.2", {"start": v(204.38, -166.93) * mm, "end": v(199.5, -159.57) * mm});
            skLineSegment(sketch, "E227.3", {"start": v(199.5, -159.57) * mm, "end": v(203.44, -151.66) * mm});
            skLineSegment(sketch, "E227.4", {"start": v(203.44, -151.66) * mm, "end": v(212.25, -151.11) * mm});
            skLineSegment(sketch, "E227.5", {"start": v(212.25, -151.11) * mm, "end": v(217.13, -158.47) * mm});
            skPoint(sketch, "E227.0.midPoint", {"position": v(215.17, -162.43) * mm});
            skPoint(sketch, "E228.0.midPoint", {"position": v(236.7, -175.4) * mm});
            skLineSegment(sketch, "E228.4", {"start": v(224.98, -164.64) * mm, "end": v(233.8, -164.09) * mm});
            skLineSegment(sketch, "E228.3", {"start": v(221.04, -172.54) * mm, "end": v(224.98, -164.64) * mm});
            skLineSegment(sketch, "E228.1", {"start": v(234.74, -179.36) * mm, "end": v(225.92, -179.9) * mm});
            skLineSegment(sketch, "E228.0", {"start": v(238.68, -171.45) * mm, "end": v(234.74, -179.36) * mm});
            skLineSegment(sketch, "E228.2", {"start": v(225.92, -179.9) * mm, "end": v(221.04, -172.54) * mm});
            skLineSegment(sketch, "E228.5", {"start": v(233.8, -164.09) * mm, "end": v(238.68, -171.45) * mm});
            skPoint(sketch, "E229.0.midPoint", {"position": v(218.2, -185.1) * mm});
            skLineSegment(sketch, "E229.4", {"start": v(206.47, -174.33) * mm, "end": v(215.29, -173.78) * mm});
            skLineSegment(sketch, "E229.3", {"start": v(202.54, -182.24) * mm, "end": v(206.47, -174.33) * mm});
            skLineSegment(sketch, "E229.1", {"start": v(216.24, -189.05) * mm, "end": v(207.42, -189.6) * mm});
            skLineSegment(sketch, "E229.0", {"start": v(220.17, -181.14) * mm, "end": v(216.24, -189.05) * mm});
            skLineSegment(sketch, "E229.2", {"start": v(207.42, -189.6) * mm, "end": v(202.54, -182.24) * mm});
            skLineSegment(sketch, "E229.5", {"start": v(215.29, -173.78) * mm, "end": v(220.17, -181.14) * mm});
            skPoint(sketch, "E230.0.midPoint", {"position": v(253.7, -163.1) * mm});
            skLineSegment(sketch, "E230.4", {"start": v(241.98, -152.34) * mm, "end": v(250.8, -151.8) * mm});
            skLineSegment(sketch, "E230.3", {"start": v(238.04, -160.25) * mm, "end": v(241.98, -152.34) * mm});
            skLineSegment(sketch, "E230.1", {"start": v(251.74, -167.06) * mm, "end": v(242.92, -167.6) * mm});
            skLineSegment(sketch, "E230.0", {"start": v(255.68, -159.15) * mm, "end": v(251.74, -167.06) * mm});
            skLineSegment(sketch, "E230.2", {"start": v(242.92, -167.6) * mm, "end": v(238.04, -160.25) * mm});
            skLineSegment(sketch, "E230.5", {"start": v(250.8, -151.8) * mm, "end": v(255.68, -159.15) * mm});
            skPoint(sketch, "E231.0.midPoint", {"position": v(273.75, -175.88) * mm});
            skLineSegment(sketch, "E231.4", {"start": v(262.02, -165.11) * mm, "end": v(270.84, -164.56) * mm});
            skLineSegment(sketch, "E231.3", {"start": v(258.09, -173.02) * mm, "end": v(262.02, -165.11) * mm});
            skLineSegment(sketch, "E231.1", {"start": v(271.79, -179.84) * mm, "end": v(262.97, -180.38) * mm});
            skLineSegment(sketch, "E231.0", {"start": v(275.72, -171.93) * mm, "end": v(271.79, -179.84) * mm});
            skLineSegment(sketch, "E231.2", {"start": v(262.97, -180.38) * mm, "end": v(258.09, -173.02) * mm});
            skLineSegment(sketch, "E231.5", {"start": v(270.84, -164.56) * mm, "end": v(275.72, -171.93) * mm});
            skPoint(sketch, "E232.0.midPoint", {"position": v(290.22, -164.39) * mm});
            skLineSegment(sketch, "E232.4", {"start": v(278.5, -153.62) * mm, "end": v(287.3, -153.07) * mm});
            skLineSegment(sketch, "E232.3", {"start": v(274.56, -161.52) * mm, "end": v(278.5, -153.62) * mm});
            skLineSegment(sketch, "E232.1", {"start": v(288.26, -168.34) * mm, "end": v(279.44, -168.89) * mm});
            skLineSegment(sketch, "E232.0", {"start": v(292.2, -160.43) * mm, "end": v(288.26, -168.34) * mm});
            skLineSegment(sketch, "E232.2", {"start": v(279.44, -168.89) * mm, "end": v(274.56, -161.52) * mm});
            skLineSegment(sketch, "E232.5", {"start": v(287.3, -153.07) * mm, "end": v(292.2, -160.43) * mm});
            skLineSegment(sketch, "E233.MirrorCS", {"start": v(337.44, -153.62) * mm, "end": v(328.62, -153.07) * mm});
            skLineSegment(sketch, "E234.MirrorCS", {"start": v(341.37, -161.52) * mm, "end": v(337.44, -153.62) * mm});
            skLineSegment(sketch, "E235.MirrorCS", {"start": v(328.62, -153.07) * mm, "end": v(323.74, -160.43) * mm});
            skPoint(sketch, "E236.MirrorP", {"position": v(325.7, -164.39) * mm});
            skLineSegment(sketch, "E237.MirrorCS", {"start": v(323.74, -160.43) * mm, "end": v(327.67, -168.34) * mm});
            skLineSegment(sketch, "E238.MirrorCS", {"start": v(327.67, -168.34) * mm, "end": v(336.5, -168.89) * mm});
            skLineSegment(sketch, "E239.MirrorCS", {"start": v(336.5, -168.89) * mm, "end": v(341.37, -161.52) * mm});
            skLineSegment(sketch, "E240.MirrorCS", {"start": v(409.46, -174.33) * mm, "end": v(400.64, -173.78) * mm});
            skLineSegment(sketch, "E241.MirrorCS", {"start": v(402.73, -166.38) * mm, "end": v(411.55, -166.93) * mm});
            skLineSegment(sketch, "E242.MirrorCS", {"start": v(364.19, -167.06) * mm, "end": v(373, -167.6) * mm});
            skLineSegment(sketch, "E243.MirrorCS", {"start": v(390.95, -164.64) * mm, "end": v(382.13, -164.09) * mm});
            skLineSegment(sketch, "E244.MirrorCS", {"start": v(400.64, -173.78) * mm, "end": v(395.76, -181.14) * mm});
            skPoint(sketch, "E245.MirrorP", {"position": v(362.22, -163.1) * mm});
            skLineSegment(sketch, "E246.MirrorCS", {"start": v(360.25, -159.15) * mm, "end": v(364.19, -167.06) * mm});
            skLineSegment(sketch, "E247.MirrorCS", {"start": v(394.89, -172.54) * mm, "end": v(390.95, -164.64) * mm});
            skLineSegment(sketch, "E248.MirrorCS", {"start": v(344.14, -179.84) * mm, "end": v(352.96, -180.38) * mm});
            skPoint(sketch, "E249.MirrorP", {"position": v(400.76, -162.43) * mm});
            skLineSegment(sketch, "E250.MirrorCS", {"start": v(373, -167.6) * mm, "end": v(377.89, -160.25) * mm});
            skLineSegment(sketch, "E251.MirrorCS", {"start": v(395.76, -181.14) * mm, "end": v(399.7, -189.05) * mm});
            skLineSegment(sketch, "E252.MirrorCS", {"start": v(377.25, -171.45) * mm, "end": v(381.19, -179.36) * mm});
            skPoint(sketch, "E253.MirrorP", {"position": v(379.22, -175.4) * mm});
            skLineSegment(sketch, "E254.MirrorCS", {"start": v(381.19, -179.36) * mm, "end": v(390, -179.9) * mm});
            skLineSegment(sketch, "E255.MirrorCS", {"start": v(382.13, -164.09) * mm, "end": v(377.25, -171.45) * mm});
            skLineSegment(sketch, "E256.MirrorCS", {"start": v(357.84, -173.02) * mm, "end": v(353.9, -165.11) * mm});
            skLineSegment(sketch, "E257.MirrorCS", {"start": v(352.96, -180.38) * mm, "end": v(357.84, -173.02) * mm});
            skLineSegment(sketch, "E258.MirrorCS", {"start": v(377.89, -160.25) * mm, "end": v(373.95, -152.34) * mm});
            skPoint(sketch, "E259.MirrorP", {"position": v(342.18, -175.88) * mm});
            skLineSegment(sketch, "E260.MirrorCS", {"start": v(390, -179.9) * mm, "end": v(394.89, -172.54) * mm});
            skLineSegment(sketch, "E261.MirrorCS", {"start": v(373.95, -152.34) * mm, "end": v(365.14, -151.8) * mm});
            skLineSegment(sketch, "E262.MirrorCS", {"start": v(340.2, -171.93) * mm, "end": v(344.14, -179.84) * mm});
            skLineSegment(sketch, "E263.MirrorCS", {"start": v(353.9, -165.11) * mm, "end": v(345.09, -164.56) * mm});
            skLineSegment(sketch, "E264.MirrorCS", {"start": v(365.14, -151.8) * mm, "end": v(360.25, -159.15) * mm});
            skLineSegment(sketch, "E265.MirrorCS", {"start": v(345.09, -164.56) * mm, "end": v(340.2, -171.93) * mm});
            skLineSegment(sketch, "E266.MirrorCS", {"start": v(399.7, -189.05) * mm, "end": v(408.51, -189.6) * mm});
            skLineSegment(sketch, "E267.MirrorCS", {"start": v(408.51, -189.6) * mm, "end": v(413.4, -182.24) * mm});
            skLineSegment(sketch, "E268.MirrorCS", {"start": v(413.4, -182.24) * mm, "end": v(409.46, -174.33) * mm});
            skLineSegment(sketch, "E269.MirrorCS", {"start": v(411.55, -166.93) * mm, "end": v(416.43, -159.57) * mm});
            skLineSegment(sketch, "E270.MirrorCS", {"start": v(416.43, -159.57) * mm, "end": v(412.5, -151.66) * mm});
            skLineSegment(sketch, "E271.MirrorCS", {"start": v(412.5, -151.66) * mm, "end": v(403.68, -151.11) * mm});
            skLineSegment(sketch, "E272.MirrorCS", {"start": v(403.68, -151.11) * mm, "end": v(398.8, -158.47) * mm});
            skLineSegment(sketch, "E273.MirrorCS", {"start": v(398.8, -158.47) * mm, "end": v(402.73, -166.38) * mm});
            skArc(sketch, "E274", {"start": v(294.45, -137.78) * mm, "mid": v(307.96, -151.73) * mm, "end": v(321.48, -137.78) * mm});
            skPoint(sketch, "E275", {"position": v(443, -157.78) * mm});
            skPoint(sketch, "E276", {"position": v(443, -161.78) * mm});
            skLineSegment(sketch, "E277", {"start": v(443, -157.78) * mm, "end": v(435, -157.78) * mm});
            skLineSegment(sketch, "E278", {"start": v(435, -157.78) * mm, "end": v(435, -161.78) * mm});
            skLineSegment(sketch, "E279", {"start": v(435, -161.78) * mm, "end": v(443, -161.78) * mm});
            skLineSegment(sketch, "E280.MirrorCS", {"start": v(180.93, -161.78) * mm, "end": v(172.93, -161.78) * mm});
            skLineSegment(sketch, "E281.MirrorCS", {"start": v(172.93, -157.78) * mm, "end": v(180.93, -157.78) * mm});
            skLineSegment(sketch, "E282.MirrorCS", {"start": v(180.93, -157.78) * mm, "end": v(180.93, -161.78) * mm});
            skPoint(sketch, "E283.orphan", {"position": v(286.93, -201.78) * mm});
            skPoint(sketch, "E284.orphan", {"position": v(329, -201.78) * mm});
            skLineSegment(sketch, "E285.trimOffspring", {"start": v(443, -161.78) * mm, "end": v(443, -201.78) * mm});
            skLineSegment(sketch, "E286.trimOffspring", {"start": v(172.93, -161.78) * mm, "end": v(172.93, -201.78) * mm});
            skLineSegment(sketch, "E287.MirrorCS", {"start": v(227.16, -211) * mm, "end": v(227.16, -226.44) * mm});
            skLineSegment(sketch, "E288.MirrorCS", {"start": v(222.96, -226.44) * mm, "end": v(222.96, -211) * mm});
            skLineSegment(sketch, "E289.MirrorCS", {"start": v(227.16, -211) * mm, "end": v(223.16, -211) * mm});
            skLineSegment(sketch, "E290.MirrorCS", {"start": v(227.16, -226.44) * mm, "end": v(223.16, -226.44) * mm});
            skLineSegment(sketch, "E291", {"start": v(392.68, -226.44) * mm, "end": v(392.68, -211) * mm});
            skLineSegment(sketch, "E292", {"start": v(388.68, -226.44) * mm, "end": v(392.68, -226.44) * mm});
            skLineSegment(sketch, "E293.trimOffspring", {"start": v(388.68, -211) * mm, "end": v(388.68, -226.44) * mm});
            skLineSegment(sketch, "E294", {"start": v(388.68, -211) * mm, "end": v(392.68, -211) * mm});
            skLineSegment(sketch, "E295", {"start": v(388.68, -218.72) * mm, "end": v(227.16, -218.72) * mm, "construction": true});
            skPoint(sketch, "E296", {"position": v(307.92, -218.72) * mm});
            skLineSegment(sketch, "E297", {"start": v(307.96, -138.21) * mm, "end": v(307.96, -268.31) * mm, "construction": true});
            skLineSegment(sketch, "E298", {"start": v(222.96, -211) * mm, "end": v(222.96, -126.94) * mm, "construction": true});
            skPoint(sketch, "E299", {"position": v(222.96, -181.95) * mm});
            skPoint(sketch, "E300", {"position": v(222.96, -201.78) * mm});
            skPoint(sketch, "E301", {"position": v(222.96, -161.95) * mm});
            skLineSegment(sketch, "E302", {"start": v(392.68, -211) * mm, "end": v(392.68, -131.14) * mm, "construction": true});
            skLineSegment(sketch, "E303", {"start": v(227.16, -211) * mm, "end": v(227.16, -120.97) * mm, "construction": true});
            skLineSegment(sketch, "E304", {"start": v(388.68, -211) * mm, "end": v(388.68, -120.97) * mm, "construction": true});
            skLineSegment(sketch, "E305", {"start": v(222.96, -161.95) * mm, "end": v(503.9, -161.95) * mm, "construction": true});
            skLineSegment(sketch, "E306", {"start": v(222.96, -181.95) * mm, "end": v(493.21, -181.95) * mm, "construction": true});
            skLineSegment(sketch, "E307.bottom", {"start": v(222.96, -161.95) * mm, "end": v(227.16, -161.95) * mm});
            skLineSegment(sketch, "E307.top", {"start": v(222.96, -181.95) * mm, "end": v(227.16, -181.95) * mm});
            skLineSegment(sketch, "E307.left", {"start": v(222.96, -161.95) * mm, "end": v(222.96, -181.95) * mm});
            skLineSegment(sketch, "E307.right", {"start": v(227.16, -161.95) * mm, "end": v(227.16, -181.95) * mm});
            skLineSegment(sketch, "E308.bottom", {"start": v(388.68, -161.95) * mm, "end": v(392.68, -161.95) * mm});
            skLineSegment(sketch, "E308.top", {"start": v(388.68, -181.95) * mm, "end": v(392.68, -181.95) * mm});
            skLineSegment(sketch, "E308.left", {"start": v(388.68, -161.95) * mm, "end": v(388.68, -181.95) * mm});
            skLineSegment(sketch, "E308.right", {"start": v(392.68, -161.95) * mm, "end": v(392.68, -181.95) * mm});
            skLineSegment(sketch, "E309", {"start": v(402.73, -166.38) * mm, "end": v(402.73, -173.9) * mm, "construction": true});
            skLineSegment(sketch, "E310", {"start": v(213.2, -166.38) * mm, "end": v(213.66, -173.88) * mm, "construction": true});
            skCircle(sketch, "E311", {"center": v(213.43, -170.13) * mm, "radius": 2 * mm});
            skCircle(sketch, "E312", {"center": v(402.73, -170.15) * mm, "radius": 2 * mm});
            skLineSegment(sketch, "E313", {"start": v(213.43, -170.13) * mm, "end": v(222.96, -170.13) * mm, "construction": true});
            skSolve(sketch);
        }
        {
            var Q0;
            Q0=makeQuery(id+"F8.imprint","IMPRINT",FACE,{"disambiguationData":[TD([[makeQuery(id+"F8.imprint","IMPRINT",EDGE,{"derivedFrom":sQuery(id+"F8.wireOp",EDGE,"E214")}),-1.0]])]});
            var Q1;
            Q1=makeQuery(id+"F8.imprint","IMPRINT",FACE,{"disambiguationData":[TD([[makeQuery(id+"F8.imprint","IMPRINT",EDGE,{"derivedFrom":sQuery(id+"F8.wireOp",EDGE,"E219.MirrorC")}),1.0]])]});
            var Q2;
            {var subQ0=sQuery(id+"F8.wireOp",EDGE,"E228.2");var subQ1=sQuery(id+"F8.wireOp",EDGE,"E228.3");var subQ2=makeQuery(id+"F8.imprint","INTERSECT",VERTEX,{"derivedFrom":[subQ1,subQ0]});Q2=makeQuery(id+"F8.imprint","IMPRINT",FACE,{"disambiguationData":[TD([[makeQuery(id+"F8.imprint","IMPRINT",EDGE,{"disambiguationData":[TD([[subQ2,-1.0]])],"derivedFrom":subQ1}),-1.0]])]});}
            var Q3;
            {var subQ0=sQuery(id+"F8.wireOp",EDGE,"E260.MirrorCS");var subQ1=sQuery(id+"F8.wireOp",EDGE,"E247.MirrorCS");var subQ2=makeQuery(id+"F8.imprint","INTERSECT",VERTEX,{"derivedFrom":[subQ1,subQ0]});Q3=makeQuery(id+"F8.imprint","IMPRINT",FACE,{"disambiguationData":[TD([[makeQuery(id+"F8.imprint","IMPRINT",EDGE,{"disambiguationData":[TD([[subQ2,-1.0]])],"derivedFrom":subQ1}),1.0]])]});}
            extrude(context, id + "F9", {"entities" : qUnion([Q0, Q1, Q2, Q3]), "depth" : 4 * mm});
        }
        {
            var Q0;
            Q0=makeQuery(id+"F8.imprint","IMPRINT",FACE,{"disambiguationData":[TD([[makeQuery(id+"F8.imprint","IMPRINT",EDGE,{"derivedFrom":sQuery(id+"F8.wireOp",EDGE,"E233.MirrorCS")}),1.0]])]});
            var Q1;
            Q1=makeQuery(id+"F8.imprint","IMPRINT",FACE,{"disambiguationData":[TD([[makeQuery(id+"F8.imprint","IMPRINT",EDGE,{"derivedFrom":sQuery(id+"F8.wireOp",EDGE,"E232.4")}),-1.0]])]});
            var Q2;
            Q2=makeQuery(id+"F8.imprint","IMPRINT",FACE,{"disambiguationData":[TD([[makeQuery(id+"F8.imprint","IMPRINT",EDGE,{"derivedFrom":sQuery(id+"F8.wireOp",EDGE,"E231.4")}),-1.0]])]});
            var Q3;
            Q3=makeQuery(id+"F8.imprint","IMPRINT",FACE,{"disambiguationData":[TD([[makeQuery(id+"F8.imprint","IMPRINT",EDGE,{"derivedFrom":sQuery(id+"F8.wireOp",EDGE,"E230.4")}),-1.0]])]});
            var Q4;
            Q4=makeQuery(id+"F8.imprint","IMPRINT",FACE,{"disambiguationData":[TD([[makeQuery(id+"F8.imprint","IMPRINT",EDGE,{"derivedFrom":sQuery(id+"F8.wireOp",EDGE,"E228.4")}),-1.0]])]});
            var Q5;
            Q5=makeQuery(id+"F8.imprint","IMPRINT",FACE,{"disambiguationData":[TD([[makeQuery(id+"F8.imprint","IMPRINT",EDGE,{"derivedFrom":sQuery(id+"F8.wireOp",EDGE,"E227.0")}),-1.0]])]});
            var Q6;
            Q6=makeQuery(id+"F8.imprint","IMPRINT",FACE,{"disambiguationData":[TD([[makeQuery(id+"F8.imprint","IMPRINT",EDGE,{"derivedFrom":sQuery(id+"F8.wireOp",EDGE,"E248.MirrorCS")}),1.0]])]});
            var Q7;
            Q7=makeQuery(id+"F8.imprint","IMPRINT",FACE,{"disambiguationData":[TD([[makeQuery(id+"F8.imprint","IMPRINT",EDGE,{"derivedFrom":sQuery(id+"F8.wireOp",EDGE,"E242.MirrorCS")}),1.0]])]});
            var Q8;
            Q8=makeQuery(id+"F8.imprint","IMPRINT",FACE,{"disambiguationData":[TD([[makeQuery(id+"F8.imprint","IMPRINT",EDGE,{"derivedFrom":sQuery(id+"F8.wireOp",EDGE,"E243.MirrorCS")}),1.0]])]});
            var Q9;
            Q9=makeQuery(id+"F8.imprint","IMPRINT",FACE,{"disambiguationData":[TD([[makeQuery(id+"F8.imprint","IMPRINT",EDGE,{"derivedFrom":sQuery(id+"F8.wireOp",EDGE,"E241.MirrorCS")}),1.0]])]});
            var Q10;
            Q10=makeQuery(id+"F8.imprint","IMPRINT",FACE,{"disambiguationData":[TD([[makeQuery(id+"F8.imprint","IMPRINT",EDGE,{"derivedFrom":sQuery(id+"F8.wireOp",EDGE,"E229.4")}),-1.0]])]});
            var Q11;
            Q11=makeQuery(id+"F8.imprint","IMPRINT",FACE,{"disambiguationData":[TD([[makeQuery(id+"F8.imprint","IMPRINT",EDGE,{"derivedFrom":sQuery(id+"F8.wireOp",EDGE,"E240.MirrorCS")}),1.0]])]});
            extrude(context, id + "F10", {"entities" : qUnion([Q0, Q1, Q2, Q3, Q4, Q5, Q6, Q7, Q8, Q9, Q10, Q11]), "operationType" : NewBodyOperationType.ADD, "depth" : 3.5 * mm});
        }
        {
            var Q0;
            Q0=qCreatedBy(makeId("Top.planeOp"),FACE);
            var sketch = newSketch(context, id + "F11", { "sketchPlane" : qUnion([Q0])});
            skCircle(sketch, "E314", {"center": v(119.17, 58.1) * mm, "radius": 2 * mm});
            skArc(sketch, "E315", {"start": v(255.65, 48.1) * mm, "mid": v(244.2, 48.35) * mm, "end": v(232.76, 48.1) * mm});
            skLineSegment(sketch, "E316.MirrorCS", {"start": v(109.17, 92.1) * mm, "end": v(109.17, 82.1) * mm});
            skCircle(sketch, "E317.MirrorC", {"center": v(119.17, 82.1) * mm, "radius": 2 * mm});
            skLineSegment(sketch, "E318", {"start": v(379.24, 92.1) * mm, "end": v(379.24, 82.3) * mm});
            skPoint(sketch, "E319.0.midPoint", {"position": v(172.95, 64.48) * mm});
            skLineSegment(sketch, "E319.4", {"start": v(161.22, 75.25) * mm, "end": v(170.03, 75.8) * mm});
            skLineSegment(sketch, "E319.3", {"start": v(157.28, 67.34) * mm, "end": v(161.22, 75.25) * mm});
            skLineSegment(sketch, "E319.1", {"start": v(170.98, 60.53) * mm, "end": v(162.16, 59.98) * mm});
            skLineSegment(sketch, "E319.0", {"start": v(174.91, 68.43) * mm, "end": v(170.98, 60.53) * mm});
            skCircle(sketch, "E319.cCircle", {"center": v(166.1, 67.89) * mm, "radius": 7.65 * mm, "construction": true});
            skLineSegment(sketch, "E319.2", {"start": v(162.16, 59.98) * mm, "end": v(157.28, 67.34) * mm});
            skLineSegment(sketch, "E319.5", {"start": v(170.03, 75.8) * mm, "end": v(174.91, 68.43) * mm});
            skPoint(sketch, "E320.0.midPoint", {"position": v(154.44, 54.79) * mm});
            skLineSegment(sketch, "E320.4", {"start": v(142.7, 65.56) * mm, "end": v(151.53, 66.1) * mm});
            skLineSegment(sketch, "E320.3", {"start": v(138.77, 57.65) * mm, "end": v(142.7, 65.56) * mm});
            skLineSegment(sketch, "E320.1", {"start": v(152.47, 50.84) * mm, "end": v(143.66, 50.29) * mm});
            skLineSegment(sketch, "E320.0", {"start": v(156.4, 58.74) * mm, "end": v(152.47, 50.84) * mm});
            skCircle(sketch, "E320.cCircle", {"center": v(147.6, 58.2) * mm, "radius": 7.65 * mm, "construction": true});
            skLineSegment(sketch, "E320.2", {"start": v(143.66, 50.29) * mm, "end": v(138.77, 57.65) * mm});
            skLineSegment(sketch, "E320.5", {"start": v(151.53, 66.1) * mm, "end": v(156.4, 58.74) * mm});
            skPoint(sketch, "E321.0.midPoint", {"position": v(189.95, 76.78) * mm});
            skLineSegment(sketch, "E321.4", {"start": v(178.21, 87.55) * mm, "end": v(187.03, 88.1) * mm});
            skLineSegment(sketch, "E321.3", {"start": v(174.28, 79.64) * mm, "end": v(178.21, 87.55) * mm});
            skLineSegment(sketch, "E321.1", {"start": v(187.98, 72.82) * mm, "end": v(179.16, 72.28) * mm});
            skLineSegment(sketch, "E321.0", {"start": v(191.91, 80.73) * mm, "end": v(187.98, 72.82) * mm});
            skCircle(sketch, "E321.cCircle", {"center": v(183.1, 80.19) * mm, "radius": 7.65 * mm, "construction": true});
            skLineSegment(sketch, "E321.2", {"start": v(179.16, 72.28) * mm, "end": v(174.28, 79.64) * mm});
            skLineSegment(sketch, "E321.5", {"start": v(187.03, 88.1) * mm, "end": v(191.91, 80.73) * mm});
            skPoint(sketch, "E322.0.midPoint", {"position": v(210, 64) * mm});
            skLineSegment(sketch, "E322.4", {"start": v(198.26, 74.78) * mm, "end": v(207.08, 75.32) * mm});
            skLineSegment(sketch, "E322.3", {"start": v(194.33, 66.87) * mm, "end": v(198.26, 74.78) * mm});
            skLineSegment(sketch, "E322.1", {"start": v(208.02, 60.05) * mm, "end": v(199.2, 59.5) * mm});
            skLineSegment(sketch, "E322.0", {"start": v(211.96, 67.96) * mm, "end": v(208.02, 60.05) * mm});
            skCircle(sketch, "E322.cCircle", {"center": v(203.14, 67.41) * mm, "radius": 7.65 * mm, "construction": true});
            skLineSegment(sketch, "E322.2", {"start": v(199.2, 59.5) * mm, "end": v(194.33, 66.87) * mm});
            skLineSegment(sketch, "E322.5", {"start": v(207.08, 75.32) * mm, "end": v(211.96, 67.96) * mm});
            skPoint(sketch, "E323.0.midPoint", {"position": v(226.46, 75.5) * mm});
            skLineSegment(sketch, "E323.4", {"start": v(214.73, 86.27) * mm, "end": v(223.55, 86.82) * mm});
            skLineSegment(sketch, "E323.3", {"start": v(210.8, 78.36) * mm, "end": v(214.73, 86.27) * mm});
            skLineSegment(sketch, "E323.1", {"start": v(224.5, 71.55) * mm, "end": v(215.68, 71) * mm});
            skLineSegment(sketch, "E323.0", {"start": v(228.43, 79.45) * mm, "end": v(224.5, 71.55) * mm});
            skCircle(sketch, "E323.cCircle", {"center": v(219.61, 78.9) * mm, "radius": 7.65 * mm, "construction": true});
            skLineSegment(sketch, "E323.2", {"start": v(215.68, 71) * mm, "end": v(210.8, 78.36) * mm});
            skLineSegment(sketch, "E323.5", {"start": v(223.55, 86.82) * mm, "end": v(228.43, 79.45) * mm});
            skLineSegment(sketch, "E324.MirrorCS", {"start": v(273.68, 86.27) * mm, "end": v(264.86, 86.82) * mm});
            skLineSegment(sketch, "E325.MirrorCS", {"start": v(277.61, 78.36) * mm, "end": v(273.68, 86.27) * mm});
            skLineSegment(sketch, "E326.MirrorCS", {"start": v(264.86, 86.82) * mm, "end": v(259.98, 79.45) * mm});
            skPoint(sketch, "E327.MirrorP", {"position": v(261.94, 75.5) * mm});
            skLineSegment(sketch, "E328.MirrorCS", {"start": v(259.98, 79.45) * mm, "end": v(263.91, 71.55) * mm});
            skLineSegment(sketch, "E329.MirrorCS", {"start": v(263.91, 71.55) * mm, "end": v(272.73, 71) * mm});
            skLineSegment(sketch, "E330.MirrorCS", {"start": v(272.73, 71) * mm, "end": v(277.61, 78.36) * mm});
            skLineSegment(sketch, "E331.MirrorCS", {"start": v(345.7, 65.56) * mm, "end": v(336.88, 66.1) * mm});
            skLineSegment(sketch, "E332.MirrorCS", {"start": v(300.43, 72.82) * mm, "end": v(309.24, 72.28) * mm});
            skLineSegment(sketch, "E333.MirrorCS", {"start": v(327.2, 75.25) * mm, "end": v(318.37, 75.8) * mm});
            skLineSegment(sketch, "E334.MirrorCS", {"start": v(336.88, 66.1) * mm, "end": v(332, 58.74) * mm});
            skPoint(sketch, "E335.MirrorP", {"position": v(298.46, 76.78) * mm});
            skLineSegment(sketch, "E336.MirrorCS", {"start": v(296.5, 80.73) * mm, "end": v(300.43, 72.82) * mm});
            skLineSegment(sketch, "E337.MirrorCS", {"start": v(331.13, 67.34) * mm, "end": v(327.2, 75.25) * mm});
            skLineSegment(sketch, "E338.MirrorCS", {"start": v(280.38, 60.05) * mm, "end": v(289.2, 59.5) * mm});
            skLineSegment(sketch, "E339.MirrorCS", {"start": v(309.24, 72.28) * mm, "end": v(314.13, 79.64) * mm});
            skLineSegment(sketch, "E340.MirrorCS", {"start": v(332, 58.74) * mm, "end": v(335.93, 50.84) * mm});
            skLineSegment(sketch, "E341.MirrorCS", {"start": v(313.5, 68.43) * mm, "end": v(317.43, 60.53) * mm});
            skPoint(sketch, "E342.MirrorP", {"position": v(315.46, 64.48) * mm});
            skLineSegment(sketch, "E343.MirrorCS", {"start": v(317.43, 60.53) * mm, "end": v(326.24, 59.98) * mm});
            skLineSegment(sketch, "E344.MirrorCS", {"start": v(318.37, 75.8) * mm, "end": v(313.5, 68.43) * mm});
            skLineSegment(sketch, "E345.MirrorCS", {"start": v(294.08, 66.87) * mm, "end": v(290.14, 74.78) * mm});
            skLineSegment(sketch, "E346.MirrorCS", {"start": v(289.2, 59.5) * mm, "end": v(294.08, 66.87) * mm});
            skLineSegment(sketch, "E347.MirrorCS", {"start": v(314.13, 79.64) * mm, "end": v(310.2, 87.55) * mm});
            skPoint(sketch, "E348.MirrorP", {"position": v(278.41, 64) * mm});
            skLineSegment(sketch, "E349.MirrorCS", {"start": v(326.24, 59.98) * mm, "end": v(331.13, 67.34) * mm});
            skLineSegment(sketch, "E350.MirrorCS", {"start": v(310.2, 87.55) * mm, "end": v(301.37, 88.1) * mm});
            skLineSegment(sketch, "E351.MirrorCS", {"start": v(276.45, 67.96) * mm, "end": v(280.38, 60.05) * mm});
            skLineSegment(sketch, "E352.MirrorCS", {"start": v(290.14, 74.78) * mm, "end": v(281.33, 75.32) * mm});
            skLineSegment(sketch, "E353.MirrorCS", {"start": v(301.37, 88.1) * mm, "end": v(296.5, 80.73) * mm});
            skLineSegment(sketch, "E354.MirrorCS", {"start": v(281.33, 75.32) * mm, "end": v(276.45, 67.96) * mm});
            skLineSegment(sketch, "E355.MirrorCS", {"start": v(335.93, 50.84) * mm, "end": v(344.75, 50.29) * mm});
            skLineSegment(sketch, "E356.MirrorCS", {"start": v(344.75, 50.29) * mm, "end": v(349.63, 57.65) * mm});
            skLineSegment(sketch, "E357.MirrorCS", {"start": v(349.63, 57.65) * mm, "end": v(345.7, 65.56) * mm});
            skLineSegment(sketch, "E358.trimOffspring", {"start": v(379.24, 78.3) * mm, "end": v(379.24, 48.1) * mm});
            skLineSegment(sketch, "E359.trimOffspring", {"start": v(109.17, 78.1) * mm, "end": v(109.17, 48.1) * mm});
            skLineSegment(sketch, "E360", {"start": v(109.17, 78.1) * mm, "end": v(109.17, 82.1) * mm});
            skLineSegment(sketch, "E361", {"start": v(379.24, 78.3) * mm, "end": v(379.24, 82.3) * mm});
            skLineSegment(sketch, "E362", {"start": v(109.17, 92.1) * mm, "end": v(379.24, 92.1) * mm});
            skLineSegment(sketch, "E363", {"start": v(109.17, 48.1) * mm, "end": v(232.76, 48.1) * mm});
            skLineSegment(sketch, "E364.trimOffspring", {"start": v(255.65, 48.1) * mm, "end": v(379.24, 48.1) * mm});
            skCircle(sketch, "E365.MirrorC", {"center": v(369.24, 58.1) * mm, "radius": 2 * mm});
            skCircle(sketch, "E366.MirrorC", {"center": v(369.24, 82.1) * mm, "radius": 2 * mm});
            skSolve(sketch);
        }
        {
            var Q0;
            Q0=makeQuery(id+"F11.imprint","IMPRINT",FACE,{"disambiguationData":[TD([[makeQuery(id+"F11.imprint","IMPRINT",EDGE,{"derivedFrom":sQuery(id+"F11.wireOp",EDGE,"E314")}),-1.0]])]});
            extrude(context, id + "F12", {"entities" : qUnion([Q0]), "depth" : 4 * mm});
        }
        {
            var Q0;
            Q0=makeQuery(id+"F11.imprint","IMPRINT",FACE,{"disambiguationData":[TD([[makeQuery(id+"F11.imprint","IMPRINT",EDGE,{"derivedFrom":sQuery(id+"F11.wireOp",EDGE,"E320.4")}),-1.0]])]});
            var Q1;
            Q1=makeQuery(id+"F11.imprint","IMPRINT",FACE,{"disambiguationData":[TD([[makeQuery(id+"F11.imprint","IMPRINT",EDGE,{"derivedFrom":sQuery(id+"F11.wireOp",EDGE,"E319.4")}),-1.0]])]});
            var Q2;
            Q2=makeQuery(id+"F11.imprint","IMPRINT",FACE,{"disambiguationData":[TD([[makeQuery(id+"F11.imprint","IMPRINT",EDGE,{"derivedFrom":sQuery(id+"F11.wireOp",EDGE,"E321.4")}),-1.0]])]});
            var Q3;
            Q3=makeQuery(id+"F11.imprint","IMPRINT",FACE,{"disambiguationData":[TD([[makeQuery(id+"F11.imprint","IMPRINT",EDGE,{"derivedFrom":sQuery(id+"F11.wireOp",EDGE,"E322.4")}),-1.0]])]});
            var Q4;
            Q4=makeQuery(id+"F11.imprint","IMPRINT",FACE,{"disambiguationData":[TD([[makeQuery(id+"F11.imprint","IMPRINT",EDGE,{"derivedFrom":sQuery(id+"F11.wireOp",EDGE,"E323.4")}),-1.0]])]});
            var Q5;
            Q5=makeQuery(id+"F11.imprint","IMPRINT",FACE,{"disambiguationData":[TD([[makeQuery(id+"F11.imprint","IMPRINT",EDGE,{"derivedFrom":sQuery(id+"F11.wireOp",EDGE,"E324.MirrorCS")}),1.0]])]});
            var Q6;
            Q6=makeQuery(id+"F11.imprint","IMPRINT",FACE,{"disambiguationData":[TD([[makeQuery(id+"F11.imprint","IMPRINT",EDGE,{"derivedFrom":sQuery(id+"F11.wireOp",EDGE,"E338.MirrorCS")}),1.0]])]});
            var Q7;
            Q7=makeQuery(id+"F11.imprint","IMPRINT",FACE,{"disambiguationData":[TD([[makeQuery(id+"F11.imprint","IMPRINT",EDGE,{"derivedFrom":sQuery(id+"F11.wireOp",EDGE,"E332.MirrorCS")}),1.0]])]});
            var Q8;
            Q8=makeQuery(id+"F11.imprint","IMPRINT",FACE,{"disambiguationData":[TD([[makeQuery(id+"F11.imprint","IMPRINT",EDGE,{"derivedFrom":sQuery(id+"F11.wireOp",EDGE,"E333.MirrorCS")}),1.0]])]});
            var Q9;
            Q9=makeQuery(id+"F11.imprint","IMPRINT",FACE,{"disambiguationData":[TD([[makeQuery(id+"F11.imprint","IMPRINT",EDGE,{"derivedFrom":sQuery(id+"F11.wireOp",EDGE,"E331.MirrorCS")}),1.0]])]});
            extrude(context, id + "F13", {"entities" : qUnion([Q0, Q1, Q2, Q3, Q4, Q5, Q6, Q7, Q8, Q9]), "operationType" : NewBodyOperationType.ADD, "depth" : 3.5 * mm});
        }
        {
            var Q0;
            Q0=qCreatedBy(makeId("Top.planeOp"),FACE);
            var sketch = newSketch(context, id + "F14", { "sketchPlane" : qUnion([Q0])});
            skCircle(sketch, "E367", {"center": v(796.44, 289.28) * mm, "radius": 2 * mm});
            skCircle(sketch, "E368", {"center": v(819.44, 289.28) * mm, "radius": 2 * mm});
            skCircle(sketch, "E369", {"center": v(807.94, 289.28) * mm, "radius": 4 * mm});
            skLineSegment(sketch, "E370", {"start": v(969.62, -46.4) * mm, "end": v(969.62, 307.18) * mm});
            skLineSegment(sketch, "E371.MirrorCS", {"start": v(646.85, -46.4) * mm, "end": v(646.85, 307.18) * mm});
            skCircle(sketch, "E372", {"center": v(656.85, 130) * mm, "radius": 2 * mm});
            skPoint(sketch, "E373", {"position": v(656.85, 290) * mm});
            skCircle(sketch, "E374", {"center": v(656.85, 290) * mm, "radius": 2 * mm});
            skPoint(sketch, "E375", {"position": v(656.85, -30) * mm});
            skCircle(sketch, "E376", {"center": v(656.85, -30) * mm, "radius": 2 * mm});
            skCircle(sketch, "E377.MirrorC", {"center": v(959.62, 130) * mm, "radius": 2 * mm});
            skCircle(sketch, "E378.MirrorC", {"center": v(959.62, -30) * mm, "radius": 2 * mm});
            skCircle(sketch, "E379.MirrorC", {"center": v(959.62, 290) * mm, "radius": 2 * mm});
            skLineSegment(sketch, "E380", {"start": v(646.85, 307.18) * mm, "end": v(790.75, 307.18) * mm});
            skLineSegment(sketch, "E381", {"start": v(646.85, -46.4) * mm, "end": v(969.62, -46.4) * mm});
            skLineSegment(sketch, "E382.trimOffspring", {"start": v(825.24, 307.18) * mm, "end": v(969.62, 307.18) * mm});
            skLineSegment(sketch, "E383", {"start": v(790.75, 307.18) * mm, "end": v(825.24, 307.18) * mm});
            skLineSegment(sketch, "E384", {"start": v(646.85, 130.4) * mm, "end": v(922.02, 130.4) * mm, "construction": true});
            skCircle(sketch, "E385.MirrorC", {"center": v(796.44, -28.5) * mm, "radius": 2 * mm});
            skCircle(sketch, "E386.MirrorC", {"center": v(807.94, -28.5) * mm, "radius": 4 * mm});
            skCircle(sketch, "E387.MirrorC", {"center": v(819.44, -28.5) * mm, "radius": 2 * mm});
            skSolve(sketch);
        }
        {
            var Q0;
            Q0=makeQuery(id+"F14.imprint","IMPRINT",FACE,{"disambiguationData":[TD([[makeQuery(id+"F14.imprint","IMPRINT",EDGE,{"derivedFrom":sQuery(id+"F14.wireOp",EDGE,"23d373e1-426d-40cf-81d0-1c8116d77816.right")}),1.0]])]});
            var Q1;
            {var subQ10=sQuery(id+"F14.wireOp",EDGE,"3c6c79d6-9cef-4f63-96dc-ad248f381b62.bottom");Q1=makeQuery(id+"F14.imprint","IMPRINT",FACE,{"disambiguationData":[TD([[makeQuery(id+"F14.imprint","IMPRINT",EDGE,{"derivedFrom":subQ10}),-1.0]])]});}
            var Q2;
            {var subQ8=sQuery(id+"F14.wireOp",EDGE,"6cf56efc-ad20-4e1a-a414-00fd335aa3e3");Q2=makeQuery(id+"F14.imprint","IMPRINT",FACE,{"disambiguationData":[TD([[makeQuery(id+"F14.imprint","IMPRINT",EDGE,{"derivedFrom":subQ8}),1.0]])]});}
            var Q3;
            {var subQ1=sQuery(id+"F14.wireOp",EDGE,"E371.MirrorCS");Q3=makeQuery(id+"F14.imprint","IMPRINT",FACE,{"disambiguationData":[TD([[makeQuery(id+"F14.imprint","IMPRINT",EDGE,{"derivedFrom":subQ1}),-1.0]])]});}
            var Q4;
            {var subQ1=sQuery(id+"F14.wireOp",EDGE,"E370");Q4=makeQuery(id+"F14.imprint","IMPRINT",FACE,{"disambiguationData":[TD([[makeQuery(id+"F14.imprint","IMPRINT",EDGE,{"derivedFrom":subQ1}),1.0]])]});}
            var Q5;
            Q5=makeQuery(id+"F14.imprint","IMPRINT",FACE,{"disambiguationData":[TD([[makeQuery(id+"F14.imprint","IMPRINT",EDGE,{"derivedFrom":sQuery(id+"F14.wireOp",EDGE,"E367")}),-1.0]])]});
            extrude(context, id + "F15", {"entities" : qUnion([Q0, Q1, Q2, Q3, Q4, Q5]), "depth" : 4 * mm});
        }
        {
            var Q0;
            Q0=qCreatedBy(makeId("Top.planeOp"),FACE);
            var sketch = newSketch(context, id + "F16", { "sketchPlane" : qUnion([Q0])});
            skPoint(sketch, "E388", {"position": v(142.81, 363.62) * mm});
            skArc(sketch, "E389", {"start": v(142.81, 363.62) * mm, "mid": v(156.1, 336.9) * mm, "end": v(182.81, 323.62) * mm});
            skCircle(sketch, "E390", {"center": v(171.81, 313.62) * mm, "radius": 2 * mm});
            skCircle(sketch, "E391", {"center": v(151.81, 313.62) * mm, "radius": 2 * mm});
            skCircle(sketch, "E392", {"center": v(132.81, 352.62) * mm, "radius": 2 * mm});
            skCircle(sketch, "E393", {"center": v(132.81, 332.62) * mm, "radius": 2 * mm});
            skArc(sketch, "E394.filletArc", {"start": v(122.81, 308.62) * mm, "mid": v(124.28, 305.09) * mm, "end": v(127.81, 303.62) * mm});
            skCircle(sketch, "E395", {"center": v(132.81, 313.62) * mm, "radius": 2.5 * mm});
            skLineSegment(sketch, "E396", {"start": v(122.81, 303.62) * mm, "end": v(122.81, 638.62) * mm});
            skLineSegment(sketch, "E397", {"start": v(502.81, 638.62) * mm, "end": v(502.81, 308.62) * mm});
            skLineSegment(sketch, "E398", {"start": v(497.81, 303.62) * mm, "end": v(127.81, 303.62) * mm});
            skArc(sketch, "E399.MirrorCS", {"start": v(482.81, 363.62) * mm, "mid": v(469.53, 336.9) * mm, "end": v(442.81, 323.62) * mm});
            skArc(sketch, "E400.MirrorCS", {"start": v(142.81, 583.62) * mm, "mid": v(156.1, 610.34) * mm, "end": v(182.81, 623.62) * mm});
            skArc(sketch, "E401.MirrorCS", {"start": v(482.81, 583.62) * mm, "mid": v(469.53, 610.34) * mm, "end": v(442.81, 623.62) * mm});
            skLineSegment(sketch, "E402", {"start": v(122.81, 638.62) * mm, "end": v(122.81, 663.62) * mm});
            skLineSegment(sketch, "E403", {"start": v(122.81, 663.62) * mm, "end": v(502.81, 663.62) * mm});
            skLineSegment(sketch, "E404", {"start": v(502.81, 663.62) * mm, "end": v(502.81, 638.62) * mm});
            skCircle(sketch, "E405", {"center": v(132.81, 385.62) * mm, "radius": 2 * mm});
            skCircle(sketch, "E406", {"center": v(132.81, 473.62) * mm, "radius": 2 * mm});
            skCircle(sketch, "E407.MirrorC", {"center": v(132.81, 561.62) * mm, "radius": 2 * mm});
            skCircle(sketch, "E408.MirrorC", {"center": v(492.81, 385.89) * mm, "radius": 2 * mm});
            skCircle(sketch, "E409.MirrorC", {"center": v(492.81, 473.62) * mm, "radius": 2 * mm});
            skCircle(sketch, "E410.MirrorC", {"center": v(492.81, 473.89) * mm, "radius": 2 * mm});
            skCircle(sketch, "E411.MirrorC", {"center": v(492.81, 561.89) * mm, "radius": 2 * mm});
            skLineSegment(sketch, "E412.trimOffspring", {"start": v(442.81, 643.62) * mm, "end": v(497.81, 643.62) * mm});
            skLineSegment(sketch, "E413", {"start": v(127.81, 643.62) * mm, "end": v(182.81, 643.62) * mm});
            skCircle(sketch, "E414.MirrorC", {"center": v(492.81, 313.62) * mm, "radius": 2.5 * mm});
            skCircle(sketch, "E415.MirrorC", {"center": v(474, 313.62) * mm, "radius": 2 * mm});
            skCircle(sketch, "E416.MirrorC", {"center": v(492.81, 327.7) * mm, "radius": 2 * mm});
            skCircle(sketch, "E417.MirrorC", {"center": v(132.81, 614.62) * mm, "radius": 2 * mm});
            skCircle(sketch, "E418.MirrorC", {"center": v(132.81, 633.62) * mm, "radius": 2.5 * mm});
            skCircle(sketch, "E419.MirrorC", {"center": v(151.81, 633.62) * mm, "radius": 2 * mm});
            skCircle(sketch, "E420.MirrorC", {"center": v(132.81, 594.62) * mm, "radius": 2 * mm});
            skCircle(sketch, "E421.MirrorC", {"center": v(474, 633.62) * mm, "radius": 2 * mm});
            skCircle(sketch, "E422.MirrorC", {"center": v(493, 614.62) * mm, "radius": 2 * mm});
            skCircle(sketch, "E423.MirrorC", {"center": v(493, 633.62) * mm, "radius": 2.5 * mm});
            skCircle(sketch, "E424.MirrorC", {"center": v(492.81, 347.7) * mm, "radius": 2 * mm});
            skCircle(sketch, "E425.MirrorC", {"center": v(454, 313.62) * mm, "radius": 2 * mm});
            skCircle(sketch, "E426.MirrorC", {"center": v(492.81, 594.62) * mm, "radius": 2 * mm});
            skCircle(sketch, "E427.MirrorC", {"center": v(454, 633.62) * mm, "radius": 2 * mm});
            skCircle(sketch, "E428.MirrorC", {"center": v(171.81, 633.62) * mm, "radius": 2 * mm});
            skLineSegment(sketch, "E429", {"start": v(122.81, 363.62) * mm, "end": v(142.81, 363.62) * mm});
            skLineSegment(sketch, "E430", {"start": v(182.81, 323.62) * mm, "end": v(182.81, 303.62) * mm});
            skLineSegment(sketch, "E431", {"start": v(142.81, 583.62) * mm, "end": v(122.81, 583.62) * mm});
            skLineSegment(sketch, "E432", {"start": v(182.81, 623.62) * mm, "end": v(182.81, 643.62) * mm});
            skLineSegment(sketch, "E433", {"start": v(442.81, 303.62) * mm, "end": v(442.81, 323.62) * mm});
            skLineSegment(sketch, "E434", {"start": v(482.81, 363.62) * mm, "end": v(502.81, 363.62) * mm});
            skLineSegment(sketch, "E435", {"start": v(442.81, 643.62) * mm, "end": v(442.81, 623.62) * mm});
            skLineSegment(sketch, "E436", {"start": v(482.81, 583.62) * mm, "end": v(502.81, 583.62) * mm});
            skLineSegment(sketch, "E437", {"start": v(502.81, 308.62) * mm, "end": v(502.81, 259.62) * mm});
            skLineSegment(sketch, "E438", {"start": v(502.81, 259.62) * mm, "end": v(122.81, 259.62) * mm});
            skLineSegment(sketch, "E439", {"start": v(122.81, 259.62) * mm, "end": v(122.81, 303.62) * mm});
            skPoint(sketch, "E440.visualSharp", {"position": v(502.81, 303.62) * mm});
            skArc(sketch, "E440.filletArc", {"start": v(497.81, 303.62) * mm, "mid": v(501.35, 305.09) * mm, "end": v(502.81, 308.62) * mm});
            skPoint(sketch, "E441.visualSharp", {"position": v(502.81, 643.62) * mm});
            skArc(sketch, "E441.filletArc", {"start": v(502.81, 638.62) * mm, "mid": v(501.35, 642.16) * mm, "end": v(497.81, 643.62) * mm});
            skPoint(sketch, "E442.visualSharp", {"position": v(122.81, 643.62) * mm});
            skArc(sketch, "E442.filletArc", {"start": v(127.81, 643.62) * mm, "mid": v(124.28, 642.16) * mm, "end": v(122.81, 638.62) * mm});
            skCircle(sketch, "E443", {"center": v(312.81, 633.62) * mm, "radius": 2 * mm});
            skCircle(sketch, "E444", {"center": v(312.81, 313.62) * mm, "radius": 2 * mm});
            skSolve(sketch);
        }
        {
            var Q0;
            {var subQ4=sQuery(id+"F16.wireOp",EDGE,"82c73330-30ee-4ce0-b7ae-c76676e96766");Q0=makeQuery(id+"F16.imprint","IMPRINT",FACE,{"disambiguationData":[TD([[makeQuery(id+"F16.imprint","IMPRINT",EDGE,{"derivedFrom":subQ4}),-1.0]])]});}
            var Q1;
            {var subQ1=sQuery(id+"F16.wireOp",EDGE,"c2653ec2-6f1e-43d4-b090-25398699ef070.MirrorCS");Q1=makeQuery(id+"F16.imprint","IMPRINT",FACE,{"disambiguationData":[TD([[makeQuery(id+"F16.imprint","IMPRINT",EDGE,{"derivedFrom":subQ1}),1.0]])]});}
            var Q2;
            {var subQ3=sQuery(id+"F16.wireOp",EDGE,"E402");Q2=makeQuery(id+"F16.imprint","IMPRINT",FACE,{"disambiguationData":[TD([[makeQuery(id+"F16.imprint","IMPRINT",EDGE,{"derivedFrom":subQ3}),-1.0]])]});}
            var Q3;
            Q3=makeQuery(id+"F16.imprint","IMPRINT",FACE,{"disambiguationData":[TD([[makeQuery(id+"F16.imprint","IMPRINT",EDGE,{"derivedFrom":sQuery(id+"F16.wireOp",EDGE,"E401.MirrorCS")}),1.0]])]});
            var Q4;
            Q4=makeQuery(id+"F16.imprint","IMPRINT",FACE,{"disambiguationData":[TD([[makeQuery(id+"F16.imprint","IMPRINT",EDGE,{"derivedFrom":sQuery(id+"F16.wireOp",EDGE,"E399.MirrorCS")}),-1.0]])]});
            var Q5;
            {var subQ1=sQuery(id+"F16.wireOp",EDGE,"E437");Q5=makeQuery(id+"F16.imprint","IMPRINT",FACE,{"disambiguationData":[TD([[makeQuery(id+"F16.imprint","IMPRINT",EDGE,{"derivedFrom":subQ1}),-1.0]])]});}
            extrude(context, id + "F17", {"entities" : qUnion([Q0, Q1, Q2, Q3, Q4, Q5]), "depth" : 4 * mm});
        }
        {
            var Q0;
            Q0=qCreatedBy(makeId("Top.planeOp"),FACE);
            var sketch = newSketch(context, id + "F18", { "sketchPlane" : qUnion([Q0])});
            skLineSegment(sketch, "E445.bottom", {"start": v(911.53, 540.54) * mm, "end": v(966.53, 540.54) * mm});
            skLineSegment(sketch, "E445.left", {"start": v(906.53, 545.54) * mm, "end": v(906.53, 600.54) * mm});
            skPoint(sketch, "E446", {"position": v(906.53, 555.54) * mm});
            skPoint(sketch, "E447", {"position": v(921.53, 600.54) * mm});
            skCircle(sketch, "E448", {"center": v(935.53, 550.54) * mm, "radius": 2 * mm});
            skPoint(sketch, "E449.visualSharp", {"position": v(906.53, 540.54) * mm});
            skArc(sketch, "E449.filletArc", {"start": v(906.53, 545.54) * mm, "mid": v(908, 542) * mm, "end": v(911.53, 540.54) * mm});
            skCircle(sketch, "E450", {"center": v(916.53, 550.54) * mm, "radius": 2.5 * mm});
            skLineSegment(sketch, "E451", {"start": v(906.53, 540.54) * mm, "end": v(1281.53, 540.54) * mm});
            skLineSegment(sketch, "E452", {"start": v(1286.53, 545.54) * mm, "end": v(1286.53, 915.54) * mm});
            skLineSegment(sketch, "E453", {"start": v(906.53, 540.54) * mm, "end": v(906.53, 915.54) * mm});
            skLineSegment(sketch, "E454", {"start": v(1281.53, 920.54) * mm, "end": v(911.53, 920.54) * mm});
            skCircle(sketch, "E455.MirrorC", {"center": v(1276.53, 550.54) * mm, "radius": 2.5 * mm});
            skCircle(sketch, "E456.MirrorC", {"center": v(1257.53, 550.54) * mm, "radius": 2 * mm});
            skCircle(sketch, "E457.MirrorC", {"center": v(916.53, 910.54) * mm, "radius": 2.5 * mm});
            skCircle(sketch, "E458.MirrorC", {"center": v(1271.53, 910.55) * mm, "radius": 2.5 * mm});
            skPoint(sketch, "E459", {"position": v(926.53, 540.54) * mm});
            skPoint(sketch, "E460.orphan", {"position": v(1096.53, 540.54) * mm});
            skLineSegment(sketch, "E461.trimOffspring", {"start": v(1096.53, 905.54) * mm, "end": v(1271.53, 905.54) * mm});
            skPoint(sketch, "E462.MirrorCS.start.orphan", {"position": v(901.53, 900.55) * mm});
            skLineSegment(sketch, "E463.trimOffspring", {"start": v(1271.53, 730.54) * mm, "end": v(1271.53, 905.54) * mm});
            skPoint(sketch, "E464.MirrorCS.start.orphan", {"position": v(1266.53, 540.54) * mm});
            skPoint(sketch, "E465.trimOffspring.end.orphan", {"position": v(921.53, 920.54) * mm});
            skPoint(sketch, "E466.orphan", {"position": v(1271.53, 920.54) * mm});
            skPoint(sketch, "E467.trimOffspring.end.orphan", {"position": v(1281.53, 900.55) * mm});
            skPoint(sketch, "E468.MirrorCS.start.orphan", {"position": v(1286.53, 555.54) * mm});
            skPoint(sketch, "E469.trimOffspring.end.orphan", {"position": v(1286.53, 560.55) * mm});
            skPoint(sketch, "E470.trimOffspring.end.orphan", {"position": v(906.53, 560.55) * mm});
            skPoint(sketch, "E471.orphan", {"position": v(1286.53, 730.54) * mm});
            skPoint(sketch, "E472.orphan", {"position": v(1281.53, 730.54) * mm});
            skPoint(sketch, "E473.orphan", {"position": v(906.53, 730.54) * mm});
            skPoint(sketch, "E474.orphan", {"position": v(1096.53, 920.54) * mm});
            skPoint(sketch, "E475.visualSharp", {"position": v(1286.53, 920.54) * mm});
            skArc(sketch, "E475.filletArc", {"start": v(1286.53, 915.54) * mm, "mid": v(1285.07, 919.08) * mm, "end": v(1281.53, 920.54) * mm});
            skPoint(sketch, "E476.visualSharp", {"position": v(906.53, 920.54) * mm});
            skArc(sketch, "E476.filletArc", {"start": v(911.53, 920.54) * mm, "mid": v(908, 919.08) * mm, "end": v(906.53, 915.54) * mm});
            skPoint(sketch, "E477.visualSharp", {"position": v(1286.53, 540.54) * mm});
            skArc(sketch, "E477.filletArc", {"start": v(1281.53, 540.54) * mm, "mid": v(1285.07, 542) * mm, "end": v(1286.53, 545.54) * mm});
            skPoint(sketch, "E478.end.orphan", {"position": v(-182644023.01, 555.54) * mm});
            skPoint(sketch, "E479.trimOffspring.start.orphan", {"position": v(1271.53, 600.54) * mm});
            skPoint(sketch, "E480.trimOffspring.start.orphan", {"position": v(182646216.07, 555.54) * mm});
            skPoint(sketch, "E481.orphan", {"position": v(182646216.07, 895.54) * mm});
            skPoint(sketch, "E482.trimOffspring.end.orphan", {"position": v(921.53, 860.55) * mm});
            skPoint(sketch, "E483.orphan", {"position": v(-182644023.01, 915.54) * mm});
            skLineSegment(sketch, "E484.MirrorCS", {"start": v(921.53, 730.54) * mm, "end": v(921.53, 905.54) * mm});
            skLineSegment(sketch, "E485.MirrorCS", {"start": v(1096.53, 905.54) * mm, "end": v(921.53, 905.54) * mm});
            skLineSegment(sketch, "E486.MirrorCS", {"start": v(1271.53, 730.54) * mm, "end": v(1271.53, 555.54) * mm});
            skLineSegment(sketch, "E487.MirrorCS", {"start": v(1096.53, 555.54) * mm, "end": v(1271.53, 555.54) * mm});
            skLineSegment(sketch, "E488.MirrorCS", {"start": v(1096.53, 555.54) * mm, "end": v(921.53, 555.54) * mm});
            skLineSegment(sketch, "E489.MirrorCS", {"start": v(921.53, 730.54) * mm, "end": v(921.53, 555.54) * mm});
            skLineSegment(sketch, "E490.0", {"start": v(926.53, 730.54) * mm, "end": v(926.53, 560.54) * mm});
            skLineSegment(sketch, "E490.1", {"start": v(1096.53, 560.54) * mm, "end": v(926.53, 560.54) * mm});
            skLineSegment(sketch, "E490.2", {"start": v(926.53, 730.54) * mm, "end": v(926.53, 900.54) * mm});
            skLineSegment(sketch, "E490.3", {"start": v(1096.53, 560.54) * mm, "end": v(1266.53, 560.54) * mm});
            skLineSegment(sketch, "E490.4", {"start": v(1096.53, 900.54) * mm, "end": v(926.53, 900.54) * mm});
            skLineSegment(sketch, "E490.5", {"start": v(1096.53, 900.54) * mm, "end": v(1266.53, 900.54) * mm});
            skLineSegment(sketch, "E490.6", {"start": v(1266.53, 730.54) * mm, "end": v(1266.53, 900.54) * mm});
            skLineSegment(sketch, "E490.7", {"start": v(1266.53, 730.54) * mm, "end": v(1266.53, 560.54) * mm});
            skSolve(sketch);
        }
        {
            var Q0;
            {var subQ6=sQuery(id+"F18.wireOp",EDGE,"E478");Q0=makeQuery(id+"F18.imprint","IMPRINT",FACE,{"disambiguationData":[TD([[makeQuery(id+"F18.imprint","IMPRINT",EDGE,{"derivedFrom":subQ6}),-1.0]])]});}
            var Q1;
            Q1=makeQuery(id+"F18.imprint","IMPRINT",FACE,{"disambiguationData":[TD([[makeQuery(id+"F18.imprint","IMPRINT",EDGE,{"derivedFrom":sQuery(id+"F18.wireOp",EDGE,"E448")}),-1.0]])]});
            var Q2;
            Q2=makeQuery(id+"F18.imprint","IMPRINT",FACE,{"disambiguationData":[TD([[makeQuery(id+"F18.imprint","IMPRINT",EDGE,{"derivedFrom":sQuery(id+"F18.wireOp",EDGE,"E461.trimOffspring")}),-1.0]])]});
            extrude(context, id + "F19", {"entities" : qUnion([Q0, Q1, Q2]), "depth" : 4 * mm});
        }
        {
            var Q0;
            Q0=makeQuery(id+"F17.opExtrude","CAP_FACE",FACE,{"disambiguationData":[OSD([sQuery(id+"F16.wireOp",EDGE,"82c73330-30ee-4ce0-b7ae-c76676e96766"),sQuery(id+"F16.wireOp",EDGE,"6159bdec-8f67-48df-ada1-b633f0472b5d"),sQuery(id+"F16.wireOp",EDGE,"E389"),sQuery(id+"F16.wireOp",EDGE,"E396"),sQuery(id+"F16.wireOp",EDGE,"64241ade-e88b-4d53-8ac9-28b0a5b8250c"),sQuery(id+"F16.wireOp",EDGE,"E397"),sQuery(id+"F16.wireOp",EDGE,"E398"),sQuery(id+"F16.wireOp",EDGE,"E399.MirrorCS"),sQuery(id+"F16.wireOp",EDGE,"753134ca-0ba6-43d0-a89f-bc8703a781450.MirrorCS"),sQuery(id+"F16.wireOp",EDGE,"d855c492-912a-4833-a90a-e979491345e50.MirrorCS"),sQuery(id+"F16.wireOp",EDGE,"c2653ec2-6f1e-43d4-b090-25398699ef070.MirrorCS"),sQuery(id+"F16.wireOp",EDGE,"E400.MirrorCS"),sQuery(id+"F16.wireOp",EDGE,"0665624d-8878-4a35-bb48-829bd46e2ff50.MirrorCS"),sQuery(id+"F16.wireOp",EDGE,"E401.MirrorCS"),sQuery(id+"F16.wireOp",EDGE,"e0f5842c-4877-4b24-b5c6-21cafd525e700.MirrorCS"),sQuery(id+"F16.wireOp",EDGE,"adf0b613-69af-4113-90ba-ee4a629042250.MirrorCS"),sQuery(id+"F16.wireOp",EDGE,"E402"),sQuery(id+"F16.wireOp",EDGE,"E403"),sQuery(id+"F16.wireOp",EDGE,"E404")])],"isStart":false});
            var sketch = newSketch(context, id + "F20", { "sketchPlane" : qUnion([Q0])});
            skPoint(sketch, "E491.visualSharp", {"position": v(-437.48, 591.17) * mm});
            skLineSegment(sketch, "E492", {"start": v(-437.48, 596.17) * mm, "end": v(-437.48, 872.33) * mm});
            skLineSegment(sketch, "E493", {"start": v(-57.48, 926.17) * mm, "end": v(-57.48, 596.17) * mm});
            skLineSegment(sketch, "E494", {"start": v(-62.48, 591.17) * mm, "end": v(-432.48, 591.17) * mm});
            skArc(sketch, "E495.MirrorCS", {"start": v(-77.54, 651) * mm, "mid": v(-90.82, 624.28) * mm, "end": v(-117.54, 611) * mm});
            skArc(sketch, "E496.MirrorCS", {"start": v(-417.48, 872.33) * mm, "mid": v(-403.58, 897.65) * mm, "end": v(-377.48, 910.02) * mm});
            skArc(sketch, "E497.MirrorCS", {"start": v(-77.48, 871.17) * mm, "mid": v(-90.76, 897.89) * mm, "end": v(-117.48, 911.17) * mm});
            skLineSegment(sketch, "E498", {"start": v(-164.87, 951.17) * mm, "end": v(-57.48, 951.17) * mm});
            skLineSegment(sketch, "E499", {"start": v(-57.48, 951.17) * mm, "end": v(-57.48, 931.17) * mm});
            skLineSegment(sketch, "E500", {"start": v(-373.35, 931.18) * mm, "end": v(-373.35, 935.17) * mm});
            skLineSegment(sketch, "E501", {"start": v(-373.35, 935.17) * mm, "end": v(-330.35, 935.17) * mm});
            skLineSegment(sketch, "E502", {"start": v(-330.35, 935.17) * mm, "end": v(-330.35, 931.17) * mm});
            skPoint(sketch, "E503.MirrorCS.start.orphan", {"position": v(-117.48, 931.17) * mm});
            skLineSegment(sketch, "E504.MirrorCS", {"start": v(-164.3, 935.17) * mm, "end": v(-164.3, 931.17) * mm});
            skLineSegment(sketch, "E505.MirrorCS", {"start": v(-121.3, 935.17) * mm, "end": v(-164.3, 935.17) * mm});
            skLineSegment(sketch, "E506.MirrorCS", {"start": v(-121.3, 931.17) * mm, "end": v(-121.3, 935.17) * mm});
            skCircle(sketch, "E507.MirrorC", {"center": v(-427.66, 902.17) * mm, "radius": 2 * mm});
            skCircle(sketch, "E508.MirrorC", {"center": v(-427.66, 921.17) * mm, "radius": 2.5 * mm});
            skCircle(sketch, "E509.MirrorC", {"center": v(-408.66, 921.17) * mm, "radius": 2 * mm});
            skCircle(sketch, "E510.MirrorC", {"center": v(-427.42, 882.18) * mm, "radius": 2 * mm});
            skCircle(sketch, "E511.MirrorC", {"center": v(-388.66, 921.17) * mm, "radius": 2 * mm});
            skCircle(sketch, "E512", {"center": v(-427.48, 761.17) * mm, "radius": 2 * mm});
            skCircle(sketch, "E513", {"center": v(-427.48, 673.17) * mm, "radius": 2 * mm});
            skCircle(sketch, "E514.MirrorC", {"center": v(-427.48, 849.17) * mm, "radius": 2 * mm});
            skCircle(sketch, "E515.MirrorC", {"center": v(-67.48, 673.17) * mm, "radius": 2 * mm});
            skCircle(sketch, "E516.MirrorC", {"center": v(-67.48, 761.17) * mm, "radius": 2 * mm});
            skCircle(sketch, "E517.MirrorC", {"center": v(-67.48, 849.17) * mm, "radius": 2 * mm});
            skCircle(sketch, "E518.MirrorC", {"center": v(-67.54, 620.17) * mm, "radius": 2 * mm});
            skCircle(sketch, "E519.MirrorC", {"center": v(-67.3, 601.17) * mm, "radius": 2.5 * mm});
            skCircle(sketch, "E520.MirrorC", {"center": v(-86.3, 601.17) * mm, "radius": 2 * mm});
            skCircle(sketch, "E521.MirrorC", {"center": v(-106.3, 601.17) * mm, "radius": 2 * mm});
            skCircle(sketch, "E522.MirrorC", {"center": v(-67.48, 882.17) * mm, "radius": 2 * mm});
            skCircle(sketch, "E523.MirrorC", {"center": v(-67.48, 902.17) * mm, "radius": 2 * mm});
            skCircle(sketch, "E524.MirrorC", {"center": v(-67.48, 921.17) * mm, "radius": 2.5 * mm});
            skCircle(sketch, "E525.MirrorC", {"center": v(-86.48, 921.17) * mm, "radius": 2 * mm});
            skCircle(sketch, "E526.MirrorC", {"center": v(-106.48, 921.17) * mm, "radius": 2 * mm});
            skLineSegment(sketch, "E527.trimOffspring", {"start": v(-117.48, 931.17) * mm, "end": v(-62.48, 931.17) * mm});
            skLineSegment(sketch, "E528", {"start": v(-117.48, 591) * mm, "end": v(-117.54, 611) * mm});
            skLineSegment(sketch, "E529", {"start": v(-117.48, 911.17) * mm, "end": v(-117.48, 931.17) * mm});
            skLineSegment(sketch, "E530", {"start": v(-77.48, 871.17) * mm, "end": v(-57.48, 871.17) * mm});
            skCircle(sketch, "E531", {"center": v(-421, 1024.4) * mm, "radius": 1.5 * mm});
            skCircle(sketch, "E532", {"center": v(-421.18, 974.46) * mm, "radius": 1.5 * mm});
            skCircle(sketch, "E533", {"center": v(-276, 974.46) * mm, "radius": 1.5 * mm});
            skCircle(sketch, "E534", {"center": v(-276, 1024.46) * mm, "radius": 1.5 * mm});
            skLineSegment(sketch, "E535", {"start": v(-437.48, 951.17) * mm, "end": v(-437.48, 1028.35) * mm});
            skLineSegment(sketch, "E536", {"start": v(-432.48, 1033.35) * mm, "end": v(-268.2, 1033.35) * mm});
            skArc(sketch, "E537", {"start": v(-263.94, 1030.98) * mm, "mid": v(-221.2, 982.64) * mm, "end": v(-164.87, 951.17) * mm});
            skPoint(sketch, "E538.visualSharp", {"position": v(-437.48, 1033.35) * mm});
            skArc(sketch, "E538.filletArc", {"start": v(-432.48, 1033.35) * mm, "mid": v(-436.01, 1031.89) * mm, "end": v(-437.48, 1028.35) * mm});
            skPoint(sketch, "E539.visualSharp", {"position": v(-265.39, 1033.35) * mm});
            skArc(sketch, "E539.filletArc", {"start": v(-263.94, 1030.98) * mm, "mid": v(-265.76, 1032.72) * mm, "end": v(-268.2, 1033.35) * mm});
            skCircle(sketch, "E540", {"center": v(-270.3, 766.4) * mm, "radius": 1.5 * mm});
            skCircle(sketch, "E541", {"center": v(-222.48, 773.77) * mm, "radius": 1.5 * mm});
            skCircle(sketch, "E542", {"center": v(-222.58, 847.1) * mm, "radius": 1.5 * mm});
            skCircle(sketch, "E543", {"center": v(-270.6, 847.1) * mm, "radius": 1.5 * mm});
            skLineSegment(sketch, "E544.top", {"start": v(-330.35, 891.17) * mm, "end": v(-373.35, 891.17) * mm});
            skLineSegment(sketch, "E544.left", {"start": v(-330.35, 931.17) * mm, "end": v(-330.35, 891.17) * mm});
            skLineSegment(sketch, "E545", {"start": v(-373.35, 931.18) * mm, "end": v(-373.35, 891.17) * mm});
            skLineSegment(sketch, "E546.MirrorCS", {"start": v(-164.3, 931.17) * mm, "end": v(-164.3, 891.17) * mm});
            skLineSegment(sketch, "E547.MirrorCS", {"start": v(-164.3, 891.17) * mm, "end": v(-122.04, 891.17) * mm});
            skLineSegment(sketch, "E548.MirrorCS", {"start": v(-121.3, 931.17) * mm, "end": v(-122.04, 891.17) * mm});
            skLineSegment(sketch, "E549", {"start": v(-437.48, 930.02) * mm, "end": v(-437.48, 951.17) * mm});
            skLineSegment(sketch, "E550", {"start": v(-377.49, 930.02) * mm, "end": v(-432.48, 930.02) * mm});
            skLineSegment(sketch, "E551", {"start": v(-417.48, 872.33) * mm, "end": v(-437.48, 872.33) * mm});
            skLineSegment(sketch, "E552", {"start": v(-377.48, 910.02) * mm, "end": v(-377.49, 930.02) * mm});
            skLineSegment(sketch, "E553", {"start": v(-437.48, 872.33) * mm, "end": v(-437.48, 925.02) * mm});
            skCircle(sketch, "E554", {"center": v(-247.48, 943.17) * mm, "radius": 3 * mm});
            skPoint(sketch, "E555.visualSharp", {"position": v(-698.98, 819.12) * mm});
            skPoint(sketch, "E556.visualSharp", {"position": v(-604.02, 688.54) * mm});
            skLineSegment(sketch, "E557.left", {"start": v(-604.02, 693.54) * mm, "end": v(-604.02, 814.12) * mm});
            skPoint(sketch, "E558.visualSharp", {"position": v(-604.02, 819.12) * mm});
            skLineSegment(sketch, "E557.bottom", {"start": v(-609.02, 688.54) * mm, "end": v(-693.98, 688.54) * mm});
            skLineSegment(sketch, "E557.top", {"start": v(-609.02, 819.12) * mm, "end": v(-693.98, 819.12) * mm});
            skCircle(sketch, "E559", {"center": v(-693.98, 693.54) * mm, "radius": 1.5 * mm});
            skArc(sketch, "E558.filletArc", {"start": v(-604.02, 814.12) * mm, "mid": v(-605.48, 817.65) * mm, "end": v(-609.02, 819.12) * mm});
            skCircle(sketch, "E560", {"center": v(-609.02, 814.12) * mm, "radius": 1.5 * mm});
            skArc(sketch, "E556.filletArc", {"start": v(-609.02, 688.54) * mm, "mid": v(-605.48, 690) * mm, "end": v(-604.02, 693.54) * mm});
            skCircle(sketch, "E561", {"center": v(-609.02, 693.54) * mm, "radius": 1.5 * mm});
            skArc(sketch, "E555.filletArc", {"start": v(-693.98, 819.12) * mm, "mid": v(-697.52, 817.65) * mm, "end": v(-698.98, 814.12) * mm});
            skCircle(sketch, "E562", {"center": v(-693.98, 814.12) * mm, "radius": 1.5 * mm});
            skLineSegment(sketch, "E557.right", {"start": v(-698.98, 693.54) * mm, "end": v(-698.98, 814.12) * mm});
            skArc(sketch, "E563.filletArc", {"start": v(-698.98, 693.54) * mm, "mid": v(-697.52, 690) * mm, "end": v(-693.98, 688.54) * mm});
            skCircle(sketch, "E564", {"center": v(-288.73, 868.53) * mm, "radius": 1.5 * mm});
            skCircle(sketch, "E565", {"center": v(-203.77, 868.53) * mm, "radius": 1.5 * mm});
            skCircle(sketch, "E566", {"center": v(-203.77, 747.95) * mm, "radius": 1.5 * mm});
            skCircle(sketch, "E567", {"center": v(-288.73, 747.95) * mm, "radius": 1.5 * mm});
            skLineSegment(sketch, "E568", {"start": v(-433.47, 941.17) * mm, "end": v(-388.66, 941.17) * mm});
            skLineSegment(sketch, "E569", {"start": v(-388.66, 941.17) * mm, "end": v(-388.66, 951.17) * mm});
            skLineSegment(sketch, "E570", {"start": v(-433.47, 951.17) * mm, "end": v(-388.66, 951.17) * mm});
            skLineSegment(sketch, "E571", {"start": v(-433.47, 941.17) * mm, "end": v(-433.47, 951.17) * mm});
            skLineSegment(sketch, "E572.MirrorCS", {"start": v(-106.3, 941.17) * mm, "end": v(-106.3, 951.17) * mm});
            skLineSegment(sketch, "E573.MirrorCS", {"start": v(-61.48, 941.17) * mm, "end": v(-106.3, 941.17) * mm});
            skLineSegment(sketch, "E574.MirrorCS", {"start": v(-61.48, 951.17) * mm, "end": v(-106.3, 951.17) * mm});
            skLineSegment(sketch, "E575.MirrorCS", {"start": v(-61.48, 941.17) * mm, "end": v(-61.48, 951.17) * mm});
            skPoint(sketch, "E576.left.start.orphan", {"position": v(-651.5, 753.83) * mm});
            skPoint(sketch, "E577.start.orphan", {"position": v(-651.5, 688.54) * mm});
            skPoint(sketch, "E578.trimOffspring.end.orphan", {"position": v(-651.5, 819.12) * mm});
            skCircle(sketch, "E579", {"center": v(-667.5, 737.83) * mm, "radius": 1.5 * mm});
            skCircle(sketch, "E580", {"center": v(-667.5, 769.83) * mm, "radius": 1.5 * mm});
            skCircle(sketch, "E581", {"center": v(-635.6, 769.88) * mm, "radius": 1.5 * mm});
            skCircle(sketch, "E582", {"center": v(-635.5, 737.83) * mm, "radius": 1.5 * mm});
            skCircle(sketch, "E583", {"center": v(-651.5, 753.83) * mm, "radius": 2.21 * mm});
            skLineSegment(sketch, "E584.trimOffspring", {"start": v(-635.6, 769.83) * mm, "end": v(-635.5, 769.83) * mm});
            skArc(sketch, "E585.trimOffspring", {"start": v(-635.6, 769.83) * mm, "mid": v(-635.6, 769.85) * mm, "end": v(-635.6, 769.88) * mm});
            skCircle(sketch, "E586.1.0.0", {"center": v(-646.3, 753.83) * mm, "radius": 2.21 * mm});
            skCircle(sketch, "E586.2.0.0", {"center": v(-641.1, 753.83) * mm, "radius": 2.21 * mm});
            skCircle(sketch, "E586.3.0.0", {"center": v(-635.9, 753.83) * mm, "radius": 2.21 * mm});
            skLineSegment(sketch, "E586.direction1", {"start": v(-651.5, 753.83) * mm, "end": v(-646.3, 753.83) * mm, "construction": true});
            skCircle(sketch, "E587.1.0.0", {"center": v(-645.63, 748) * mm, "radius": 2.21 * mm});
            skCircle(sketch, "E587.2.0.0", {"center": v(-639.76, 742.18) * mm, "radius": 2.21 * mm});
            skLineSegment(sketch, "E587.direction1", {"start": v(-651.5, 753.83) * mm, "end": v(-645.63, 748) * mm, "construction": true});
            skCircle(sketch, "E588.1.0.0", {"center": v(-651.49, 748.85) * mm, "radius": 2.21 * mm});
            skCircle(sketch, "E588.2.0.0", {"center": v(-651.47, 743.86) * mm, "radius": 2.21 * mm});
            skCircle(sketch, "E588.3.0.0", {"center": v(-651.46, 738.88) * mm, "radius": 2.21 * mm});
            skLineSegment(sketch, "E588.direction1", {"start": v(-651.5, 753.83) * mm, "end": v(-651.49, 748.85) * mm, "construction": true});
            skCircle(sketch, "E589.MirrorC", {"center": v(-651.49, 758.81) * mm, "radius": 2.21 * mm});
            skCircle(sketch, "E590.MirrorC", {"center": v(-651.47, 763.8) * mm, "radius": 2.21 * mm});
            skCircle(sketch, "E591.MirrorC", {"center": v(-651.46, 768.78) * mm, "radius": 2.21 * mm});
            skCircle(sketch, "E592.MirrorC", {"center": v(-645.63, 759.66) * mm, "radius": 2.21 * mm});
            skCircle(sketch, "E593.MirrorC", {"center": v(-639.76, 765.48) * mm, "radius": 2.21 * mm});
            skCircle(sketch, "E594.MirrorC", {"center": v(-657.34, 747.97) * mm, "radius": 2.21 * mm});
            skCircle(sketch, "E595.MirrorC", {"center": v(-656.7, 753.8) * mm, "radius": 2.21 * mm});
            skCircle(sketch, "E596.MirrorC", {"center": v(-657.4, 759.62) * mm, "radius": 2.21 * mm});
            skCircle(sketch, "E597.MirrorC", {"center": v(-661.9, 753.77) * mm, "radius": 2.21 * mm});
            skCircle(sketch, "E598.MirrorC", {"center": v(-663.17, 742.11) * mm, "radius": 2.21 * mm});
            skCircle(sketch, "E599.MirrorC", {"center": v(-663.3, 765.42) * mm, "radius": 2.21 * mm});
            skCircle(sketch, "E600.MirrorC", {"center": v(-667.1, 753.74) * mm, "radius": 2.21 * mm});
            skCircle(sketch, "E601", {"center": v(-67.54, 640.17) * mm, "radius": 2 * mm});
            skCircle(sketch, "E602.MirrorC", {"center": v(-286.48, 995.97) * mm, "radius": 10 * mm});
            skArc(sketch, "E603.MirrorCS", {"start": v(-417.42, 651) * mm, "mid": v(-404.13, 624.28) * mm, "end": v(-377.42, 611) * mm});
            skLineSegment(sketch, "E604.MirrorCS", {"start": v(-377.48, 591) * mm, "end": v(-377.42, 611) * mm});
            skLineSegment(sketch, "E605", {"start": v(-417.42, 651) * mm, "end": v(-437.48, 651) * mm});
            skLineSegment(sketch, "E606", {"start": v(-77.54, 651) * mm, "end": v(-57.48, 651) * mm});
            skCircle(sketch, "E607.MirrorC", {"center": v(-388.66, 601.17) * mm, "radius": 2 * mm});
            skCircle(sketch, "E608.MirrorC", {"center": v(-427.66, 601.17) * mm, "radius": 2.5 * mm});
            skCircle(sketch, "E609.MirrorC", {"center": v(-427.42, 620.17) * mm, "radius": 2 * mm});
            skCircle(sketch, "E610.MirrorC", {"center": v(-427.42, 640.17) * mm, "radius": 2 * mm});
            skCircle(sketch, "E611.MirrorC", {"center": v(-408.66, 601.17) * mm, "radius": 2 * mm});
            skCircle(sketch, "E612", {"center": v(-247.48, 601.17) * mm, "radius": 2 * mm});
            skArc(sketch, "E613.filletArc", {"start": v(-437.48, 596.17) * mm, "mid": v(-436.01, 592.64) * mm, "end": v(-432.48, 591.17) * mm});
            skPoint(sketch, "E614.visualSharp", {"position": v(-57.48, 591.17) * mm});
            skArc(sketch, "E614.filletArc", {"start": v(-62.48, 591.17) * mm, "mid": v(-58.94, 592.64) * mm, "end": v(-57.48, 596.17) * mm});
            skPoint(sketch, "E615.visualSharp", {"position": v(-57.48, 931.17) * mm});
            skArc(sketch, "E615.filletArc", {"start": v(-57.48, 926.17) * mm, "mid": v(-58.94, 929.7) * mm, "end": v(-62.48, 931.17) * mm});
            skPoint(sketch, "E616.visualSharp", {"position": v(-437.48, 930.02) * mm});
            skArc(sketch, "E616.filletArc", {"start": v(-432.48, 930.02) * mm, "mid": v(-436.01, 928.56) * mm, "end": v(-437.48, 925.02) * mm});
            skLineSegment(sketch, "E617", {"start": v(-437.48, 930.02) * mm, "end": v(-437.48, 925.02) * mm});
            skLineSegment(sketch, "E618", {"start": v(-57.48, 931.17) * mm, "end": v(-57.48, 926.17) * mm});
            skLineSegment(sketch, "E619.bottom", {"start": v(-409.9, 1013.6) * mm, "end": v(-311.77, 1013.6) * mm});
            skLineSegment(sketch, "E619.top", {"start": v(-409.9, 972.89) * mm, "end": v(-311.77, 972.89) * mm});
            skLineSegment(sketch, "E619.left", {"start": v(-409.9, 1013.6) * mm, "end": v(-409.9, 972.89) * mm});
            skLineSegment(sketch, "E619.right", {"start": v(-311.77, 1013.6) * mm, "end": v(-311.77, 972.89) * mm});
            skLineSegment(sketch, "E620.bottom", {"start": v(-1331.98, 846.7) * mm, "end": v(-1233.84, 846.7) * mm});
            skLineSegment(sketch, "E620.top", {"start": v(-1331.98, 805.99) * mm, "end": v(-1233.84, 805.99) * mm});
            skPoint(sketch, "E621.visualSharp", {"position": v(-1359.55, 866.45) * mm});
            skPoint(sketch, "E622.visualSharp", {"position": v(-1187.46, 866.45) * mm});
            skLineSegment(sketch, "E623", {"start": v(-1359.55, 424.28) * mm, "end": v(-1359.55, 861.45) * mm});
            skLineSegment(sketch, "E624", {"start": v(-1354.55, 866.45) * mm, "end": v(-1192.46, 866.45) * mm});
            skCircle(sketch, "E625", {"center": v(-1250.66, 605.61) * mm, "radius": 1.5 * mm});
            skCircle(sketch, "E626.MirrorC", {"center": v(-1208.56, 829.07) * mm, "radius": 10 * mm});
            skCircle(sketch, "E627", {"center": v(-1231.94, 700.37) * mm, "radius": 1.5 * mm});
            skCircle(sketch, "E628", {"center": v(-1198.08, 807.56) * mm, "radius": 1.5 * mm});
            skCircle(sketch, "E629", {"center": v(-1231.94, 579.79) * mm, "radius": 1.5 * mm});
            skCircle(sketch, "E630", {"center": v(-1250.75, 678.95) * mm, "radius": 1.5 * mm});
            skCircle(sketch, "E631", {"center": v(-1316.9, 700.37) * mm, "radius": 1.5 * mm});
            skCircle(sketch, "E632", {"center": v(-1298.78, 678.95) * mm, "radius": 1.5 * mm});
            skLineSegment(sketch, "E620.left", {"start": v(-1331.98, 846.7) * mm, "end": v(-1331.98, 805.99) * mm});
            skCircle(sketch, "E633", {"center": v(-1343.26, 807.56) * mm, "radius": 1.5 * mm});
            skLineSegment(sketch, "E620.right", {"start": v(-1233.84, 846.7) * mm, "end": v(-1233.84, 805.99) * mm});
            skCircle(sketch, "E634", {"center": v(-1343.08, 857.51) * mm, "radius": 1.5 * mm});
            skCircle(sketch, "E635", {"center": v(-1198.08, 857.56) * mm, "radius": 1.5 * mm});
            skLineSegment(sketch, "E636", {"start": v(-1187.46, 424.28) * mm, "end": v(-1359.55, 424.28) * mm});
            skLineSegment(sketch, "E637", {"start": v(-1187.46, 861.45) * mm, "end": v(-1187.46, 424.28) * mm});
            skCircle(sketch, "E638", {"center": v(-1316.82, 579.7) * mm, "radius": 1.5 * mm});
            skCircle(sketch, "E639", {"center": v(-1298.4, 598.14) * mm, "radius": 1.5 * mm});
            skArc(sketch, "E640.filletArc", {"start": v(-1187.46, 861.45) * mm, "mid": v(-1188.93, 864.99) * mm, "end": v(-1192.46, 866.45) * mm});
            skArc(sketch, "E641.filletArc", {"start": v(-1354.55, 866.45) * mm, "mid": v(-1358.09, 864.99) * mm, "end": v(-1359.55, 861.45) * mm});
            skCircle(sketch, "E642", {"center": v(-1273.5, 776.28) * mm, "radius": 3 * mm});
            skCircle(sketch, "E643", {"center": v(-1345.1, 754.28) * mm, "radius": 2 * mm});
            skCircle(sketch, "E644.MirrorC", {"center": v(-1201.92, 754.28) * mm, "radius": 2 * mm});
            skCircle(sketch, "E645.MirrorC", {"center": v(-1345.1, 434.28) * mm, "radius": 2 * mm});
            skCircle(sketch, "E646.MirrorC", {"center": v(-1201.92, 434.28) * mm, "radius": 2 * mm});
            skSolve(sketch);
        }
        {
            var Q0;
            {var subQ4=sQuery(id+"F20.wireOp",EDGE,"274de717-3da0-4c64-9ed4-fe21729b6c2f");Q0=makeQuery(id+"F20.imprint","IMPRINT",FACE,{"disambiguationData":[TD([[makeQuery(id+"F20.imprint","IMPRINT",EDGE,{"derivedFrom":subQ4}),-1.0]])]});}
            var Q1;
            Q1=makeQuery(id+"F20.imprint","IMPRINT",FACE,{"disambiguationData":[TD([[makeQuery(id+"F20.imprint","IMPRINT",EDGE,{"derivedFrom":sQuery(id+"F20.wireOp",EDGE,"E495.MirrorCS")}),-1.0]])]});
            var Q2;
            {var subQ4=sQuery(id+"F20.wireOp",EDGE,"1e5e7644-ac6b-445a-a06a-048c4de03991");Q2=makeQuery(id+"F20.imprint","IMPRINT",FACE,{"disambiguationData":[TD([[makeQuery(id+"F20.imprint","IMPRINT",EDGE,{"derivedFrom":subQ4}),-1.0]])]});}
            var Q3;
            {var subQ3=sQuery(id+"F20.wireOp",EDGE,"274de717-3da0-4c64-9ed4-fe21729b6c2f");Q3=makeQuery(id+"F20.imprint","IMPRINT",FACE,{"disambiguationData":[TD([[makeQuery(id+"F20.imprint","IMPRINT",EDGE,{"derivedFrom":subQ3}),-1.0]])]});}
            var Q4;
            Q4=makeQuery(id+"F20.imprint","IMPRINT",FACE,{"disambiguationData":[TD([[makeQuery(id+"F20.imprint","IMPRINT",EDGE,{"derivedFrom":sQuery(id+"F20.wireOp",EDGE,"E531")}),1.0]])]});
            var Q5;
            Q5=makeQuery(id+"F20.imprint","IMPRINT",FACE,{"disambiguationData":[TD([[makeQuery(id+"F20.imprint","IMPRINT",EDGE,{"derivedFrom":sQuery(id+"F20.wireOp",EDGE,"E620.bottom")}),1.0]])]});
            extrude(context, id + "F21", {"entities" : qUnion([Q0, Q1, Q2, Q3, Q4, Q5]), "depth" : 4 * mm});
        }
        {
            var Q0;
            {var subQ12=sQuery(id+"F20.wireOp",EDGE,"274de717-3da0-4c64-9ed4-fe21729b6c2f");Q0=makeQuery(id+"F20.imprint","IMPRINT",FACE,{"disambiguationData":[TD([[makeQuery(id+"F20.imprint","IMPRINT",EDGE,{"derivedFrom":subQ12}),-1.0]])]});}
            var Q1;
            {var subQ8=sQuery(id+"F20.wireOp",EDGE,"1e5e7644-ac6b-445a-a06a-048c4de03991");Q1=makeQuery(id+"F20.imprint","IMPRINT",FACE,{"disambiguationData":[TD([[makeQuery(id+"F20.imprint","IMPRINT",EDGE,{"derivedFrom":subQ8}),-1.0]])]});}
            var Q2;
            Q2=makeQuery(id+"F20.imprint","IMPRINT",FACE,{"disambiguationData":[TD([[makeQuery(id+"F20.imprint","IMPRINT",EDGE,{"derivedFrom":sQuery(id+"F20.wireOp",EDGE,"E495.MirrorCS")}),-1.0]])]});
            extrude(context, id + "F22", {"entities" : qUnion([Q0, Q1, Q2]), "operationType" : NewBodyOperationType.ADD, "depth" : 4 * mm});
        }
        {
            var Q0;
            Q0=makeQuery(id+"F20.imprint","IMPRINT",FACE,{"disambiguationData":[TD([[makeQuery(id+"F20.imprint","IMPRINT",EDGE,{"derivedFrom":sQuery(id+"F20.wireOp",EDGE,"E557.left")}),1.0]])]});
            extrude(context, id + "F23", {"entities" : qUnion([Q0]), "depth" : 4 * mm});
        }
        {
            var Q0;
            Q0=qCreatedBy(makeId("Top.planeOp"),FACE);
            var sketch = newSketch(context, id + "F24", { "sketchPlane" : qUnion([Q0])});
            skLineSegment(sketch, "E647.bottom", {"start": v(-974.65, 66.8) * mm, "end": v(-646.65, 66.8) * mm});
            skLineSegment(sketch, "E647.top", {"start": v(-974.65, -273.2) * mm, "end": v(-646.65, -273.2) * mm});
            skLineSegment(sketch, "E647.left", {"start": v(-974.65, 66.8) * mm, "end": v(-974.65, -273.2) * mm});
            skLineSegment(sketch, "E647.right", {"start": v(-646.65, 66.8) * mm, "end": v(-646.65, -273.2) * mm});
            skPoint(sketch, "E648", {"position": v(-646.65, -253.2) * mm});
            skLineSegment(sketch, "E649", {"start": v(-646.65, -253.2) * mm, "end": v(-974.65, -253.2) * mm, "construction": true});
            skPoint(sketch, "E650", {"position": v(-666.65, -273.2) * mm});
            skLineSegment(sketch, "E651", {"start": v(-666.65, -273.2) * mm, "end": v(-666.65, 66.8) * mm, "construction": true});
            skLineSegment(sketch, "E652.MirrorCS", {"start": v(-954.65, -273.2) * mm, "end": v(-954.65, 56.8) * mm, "construction": true});
            skLineSegment(sketch, "E653.MirrorCS", {"start": v(-646.65, 46.8) * mm, "end": v(-974.65, 46.8) * mm, "construction": true});
            skLineSegment(sketch, "E654", {"start": v(-974.65, -253.2) * mm, "end": v(-954.65, -253.2) * mm});
            skLineSegment(sketch, "E655", {"start": v(-954.65, -253.2) * mm, "end": v(-954.65, 46.8) * mm});
            skLineSegment(sketch, "E656", {"start": v(-954.65, 46.8) * mm, "end": v(-974.65, 46.8) * mm});
            skLineSegment(sketch, "E657", {"start": v(-646.65, -253.2) * mm, "end": v(-666.65, -253.2) * mm});
            skLineSegment(sketch, "E658", {"start": v(-666.65, -253.2) * mm, "end": v(-666.65, 46.8) * mm});
            skLineSegment(sketch, "E659", {"start": v(-666.65, 46.8) * mm, "end": v(-646.65, 46.8) * mm});
            skLineSegment(sketch, "E660.bottom", {"start": v(-1090.94, -273.2) * mm, "end": v(-1150.94, -273.2) * mm});
            skLineSegment(sketch, "E660.top", {"start": v(-1090.94, 66.8) * mm, "end": v(-1150.94, 66.8) * mm});
            skLineSegment(sketch, "E660.left", {"start": v(-1090.94, -273.2) * mm, "end": v(-1090.94, 66.8) * mm});
            skLineSegment(sketch, "E660.right", {"start": v(-1150.94, -273.2) * mm, "end": v(-1150.94, 66.8) * mm});
            skSolve(sketch);
        }
        {
            var Q0;
            Q0=makeQuery(id+"F24.imprint","IMPRINT",FACE,{"disambiguationData":[TD([[makeQuery(id+"F24.imprint","IMPRINT",EDGE,{"derivedFrom":sQuery(id+"F24.wireOp",EDGE,"E647.bottom")}),-1.0]])]});
            extrude(context, id + "F25", {"entities" : qUnion([Q0]), "depth" : 18 * mm});
        }
        {
            var Q0;
            Q0=makeQuery(id+"F24.imprint","IMPRINT",FACE,{"disambiguationData":[TD([[makeQuery(id+"F24.imprint","IMPRINT",EDGE,{"derivedFrom":sQuery(id+"F24.wireOp",EDGE,"E660.bottom")}),-1.0]])]});
            extrude(context, id + "F26", {"entities" : qUnion([Q0]), "depth" : 2 * mm});
        }
    });
